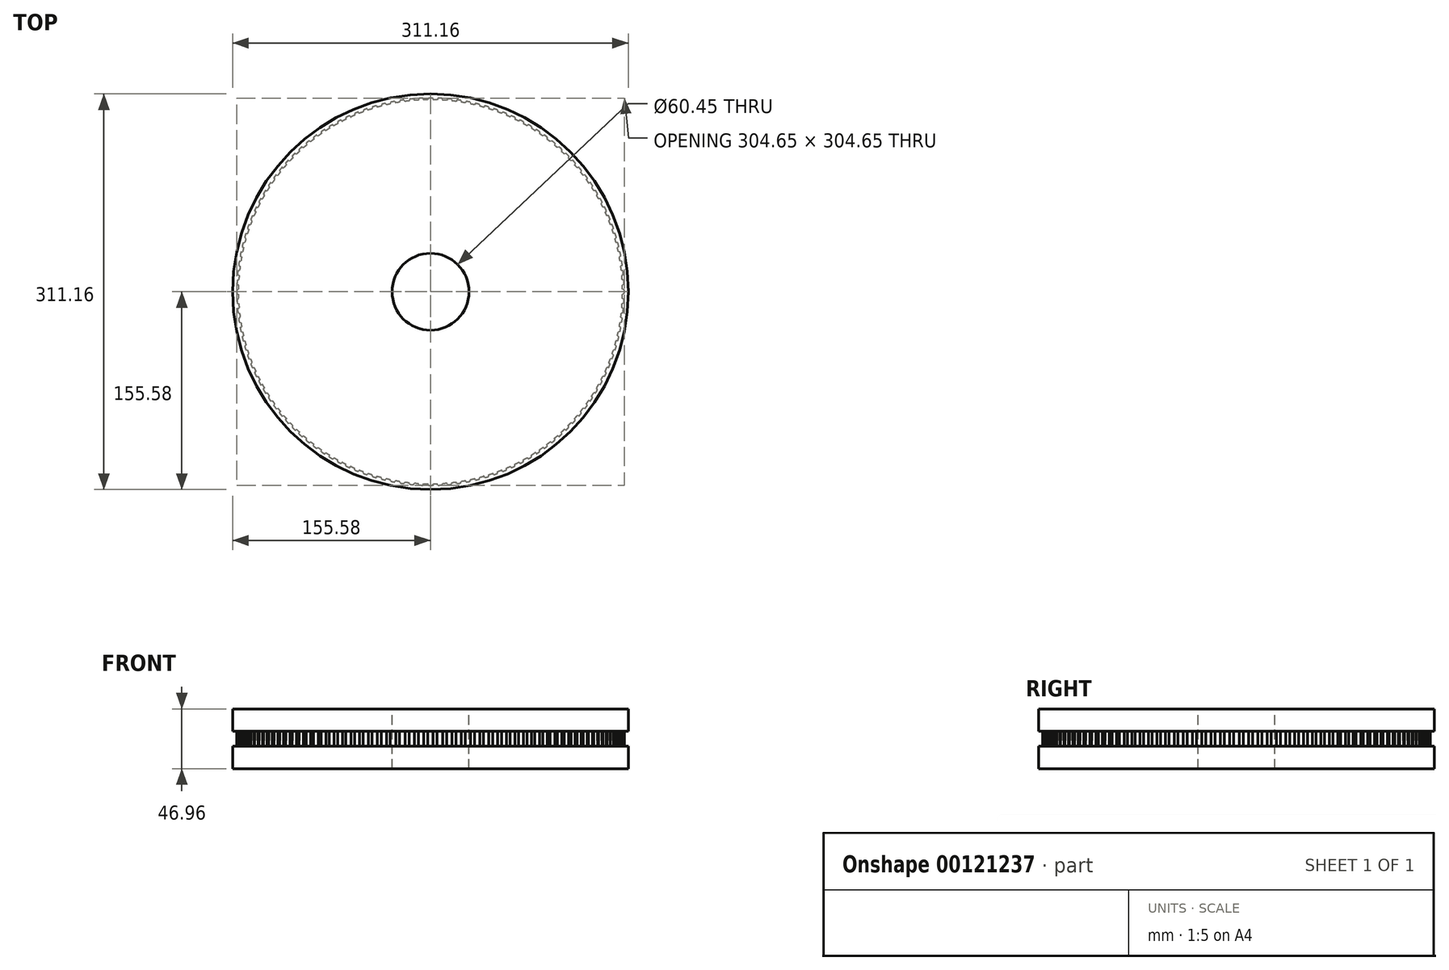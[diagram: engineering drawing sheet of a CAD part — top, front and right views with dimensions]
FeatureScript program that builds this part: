
annotation { "Feature Type Name" : "Feature", "Feature Type Description" : "" }
export const myFeature = defineFeature(function(context is Context, id is Id, definition is map)
    precondition{}
    {
        {
            var Q0;
            Q0=qCreatedBy(makeId("Top.planeOp"),FACE);
            var sketch = newSketch(context, id + "F0", { "sketchPlane" : qUnion([Q0])});
            skCircle(sketch, "E0", {"center": v(0, 0) * mm, "radius": 151 * mm});
            skSolve(sketch);
        }
        {
            var Q0;
            Q0=qSketchRegion(id+"F0",true);
            extrude(context, id + "F1", {"entities" : qUnion([Q0]), "depth" : 11.9 * mm});
        }
        {
            var Q0;
            Q0=qCreatedBy(makeId("Top.planeOp"),FACE);
            var sketch = newSketch(context, id + "F2", { "sketchPlane" : qUnion([Q0])});
            skLineSegment(sketch, "E1", {"start": v(0, -0.08) * mm, "end": v(0, 183.08) * mm, "construction": true});
            skArc(sketch, "E2", {"start": v(1.26, 152.32) * mm, "mid": v(0, 152.32) * mm, "end": v(-1.26, 152.32) * mm});
            skLineSegment(sketch, "E3", {"start": v(-1.6, 152.1) * mm, "end": v(-2.1, 151.02) * mm});
            skLineSegment(sketch, "E4", {"start": v(1.6, 152.1) * mm, "end": v(2.1, 151.02) * mm});
            skPoint(sketch, "E5.visualSharp", {"position": v(-1.5, 152.32) * mm});
            skArc(sketch, "E5.filletArc", {"start": v(-1.26, 152.32) * mm, "mid": v(-1.46, 152.26) * mm, "end": v(-1.6, 152.1) * mm});
            skPoint(sketch, "E6.visualSharp", {"position": v(1.5, 152.32) * mm});
            skArc(sketch, "E6.filletArc", {"start": v(1.6, 152.1) * mm, "mid": v(1.46, 152.26) * mm, "end": v(1.26, 152.32) * mm});
            skArc(sketch, "E7", {"start": v(-2.27, 150.9) * mm, "mid": v(-2.17, 150.94) * mm, "end": v(-2.1, 151.02) * mm});
            skArc(sketch, "E8", {"start": v(2.1, 151.02) * mm, "mid": v(2.17, 150.94) * mm, "end": v(2.27, 150.9) * mm});
            skPoint(sketch, "E9.orphan", {"position": v(2.15, 150.91) * mm});
            skArc(sketch, "E10", {"start": v(-2.27, 150.9) * mm, "mid": v(0, 150.67) * mm, "end": v(2.27, 150.9) * mm});
            skSolve(sketch);
        }
        {
            var Q0;
            Q0=makeQuery(id+"F2.imprint","IMPRINT",FACE,{"disambiguationData":[TD([[makeQuery(id+"F2.imprint","IMPRINT",EDGE,{"derivedFrom":sQuery(id+"F2.wireOp",EDGE,"E2")}),1.0]])]});
            var Q1;
            Q1=makeQuery(id+"F2.imprint","IMPRINT",FACE,{"disambiguationData":[TD([[makeQuery(id+"F2.imprint","IMPRINT",EDGE,{"derivedFrom":sQuery(id+"F2.wireOp",EDGE,"bbfa1fc5-6552-4957-9194-8f10230bb92c.0")}),1.0]])]});
            var Q2;
            Q2=makeQuery(id+"F1.opExtrude","CAP_FACE",FACE,{"disambiguationData":[OSD([sQuery(id+"F0.wireOp",EDGE,"E0")])],"isStart":false});
            extrude(context, id + "F3", {"entities" : qUnion([Q0, Q1]), "endBound" : BoundingType.UP_TO_SURFACE, "endBoundEntityFace" : qUnion([Q2]), "depth" : 25.4 * mm});
        }
        {
            var Q0;
            Q0=qCreatedBy(makeId("Front.planeOp"),FACE);
            var sketch = newSketch(context, id + "F4", { "sketchPlane" : qUnion([Q0])});
            skLineSegment(sketch, "E11", {"start": v(0, 74.48) * mm, "end": v(0, -67.78) * mm, "construction": true});
            skSolve(sketch);
        }
        {
            var Q0;
            Q0=makeQuery(id+"F3.opExtrude","SWEPT_BODY",BODY,{"disambiguationData":[OSD([sQuery(id+"F2.wireOp",EDGE,"E2"),sQuery(id+"F2.wireOp",EDGE,"E3"),sQuery(id+"F2.wireOp",EDGE,"E4"),sQuery(id+"F2.wireOp",EDGE,"E5.filletArc"),sQuery(id+"F2.wireOp",EDGE,"E6.filletArc"),sQuery(id+"F2.wireOp",EDGE,"E7"),sQuery(id+"F2.wireOp",EDGE,"E8"),sQuery(id+"F2.wireOp",EDGE,"E10")])]});
            var Q1;
            Q1=sQuery(id+"F4.wireOp",EDGE,"E11");
            circularPattern(context, id + "F5", {"entities" : qUnion([Q0]), "axis" : qUnion([Q1]), "angle" : 360 * degree, "instanceCount" : 128, "equalSpace" : true});
        }
        {
            var Q0;
            Q0=makeQuery(id+"F1.opExtrude","SWEPT_BODY",BODY,{"disambiguationData":[OSD([sQuery(id+"F0.wireOp",EDGE,"E0")])]});
            var Q1;
            Q1=makeQuery(id+"F3.opExtrude","SWEPT_BODY",BODY,{"disambiguationData":[OSD([sQuery(id+"F2.wireOp",EDGE,"E2"),sQuery(id+"F2.wireOp",EDGE,"E3"),sQuery(id+"F2.wireOp",EDGE,"E4"),sQuery(id+"F2.wireOp",EDGE,"E5.filletArc"),sQuery(id+"F2.wireOp",EDGE,"E6.filletArc"),sQuery(id+"F2.wireOp",EDGE,"E7"),sQuery(id+"F2.wireOp",EDGE,"E8"),sQuery(id+"F2.wireOp",EDGE,"E10")])]});
            var Q2;
            Q2=makeQuery(id+"F5.opPattern","COPY",BODY,{"derivedFrom":makeQuery(id+"F3.opExtrude","SWEPT_BODY",BODY,{"disambiguationData":[OSD([sQuery(id+"F2.wireOp",EDGE,"E2"),sQuery(id+"F2.wireOp",EDGE,"E3"),sQuery(id+"F2.wireOp",EDGE,"E4"),sQuery(id+"F2.wireOp",EDGE,"E5.filletArc"),sQuery(id+"F2.wireOp",EDGE,"E6.filletArc"),sQuery(id+"F2.wireOp",EDGE,"E7"),sQuery(id+"F2.wireOp",EDGE,"E8"),sQuery(id+"F2.wireOp",EDGE,"E10")])]}),"instanceName":"1"});
            var Q3;
            Q3=makeQuery(id+"F5.opPattern","COPY",BODY,{"derivedFrom":makeQuery(id+"F3.opExtrude","SWEPT_BODY",BODY,{"disambiguationData":[OSD([sQuery(id+"F2.wireOp",EDGE,"E2"),sQuery(id+"F2.wireOp",EDGE,"E3"),sQuery(id+"F2.wireOp",EDGE,"E4"),sQuery(id+"F2.wireOp",EDGE,"E5.filletArc"),sQuery(id+"F2.wireOp",EDGE,"E6.filletArc"),sQuery(id+"F2.wireOp",EDGE,"E7"),sQuery(id+"F2.wireOp",EDGE,"E8"),sQuery(id+"F2.wireOp",EDGE,"E10")])]}),"instanceName":"2"});
            var Q4;
            Q4=makeQuery(id+"F5.opPattern","COPY",BODY,{"derivedFrom":makeQuery(id+"F3.opExtrude","SWEPT_BODY",BODY,{"disambiguationData":[OSD([sQuery(id+"F2.wireOp",EDGE,"E2"),sQuery(id+"F2.wireOp",EDGE,"E3"),sQuery(id+"F2.wireOp",EDGE,"E4"),sQuery(id+"F2.wireOp",EDGE,"E5.filletArc"),sQuery(id+"F2.wireOp",EDGE,"E6.filletArc"),sQuery(id+"F2.wireOp",EDGE,"E7"),sQuery(id+"F2.wireOp",EDGE,"E8"),sQuery(id+"F2.wireOp",EDGE,"E10")])]}),"instanceName":"3"});
            var Q5;
            Q5=makeQuery(id+"F5.opPattern","COPY",BODY,{"derivedFrom":makeQuery(id+"F3.opExtrude","SWEPT_BODY",BODY,{"disambiguationData":[OSD([sQuery(id+"F2.wireOp",EDGE,"E2"),sQuery(id+"F2.wireOp",EDGE,"E3"),sQuery(id+"F2.wireOp",EDGE,"E4"),sQuery(id+"F2.wireOp",EDGE,"E5.filletArc"),sQuery(id+"F2.wireOp",EDGE,"E6.filletArc"),sQuery(id+"F2.wireOp",EDGE,"E7"),sQuery(id+"F2.wireOp",EDGE,"E8"),sQuery(id+"F2.wireOp",EDGE,"E10")])]}),"instanceName":"4"});
            var Q6;
            Q6=makeQuery(id+"F5.opPattern","COPY",BODY,{"derivedFrom":makeQuery(id+"F3.opExtrude","SWEPT_BODY",BODY,{"disambiguationData":[OSD([sQuery(id+"F2.wireOp",EDGE,"E2"),sQuery(id+"F2.wireOp",EDGE,"E3"),sQuery(id+"F2.wireOp",EDGE,"E4"),sQuery(id+"F2.wireOp",EDGE,"E5.filletArc"),sQuery(id+"F2.wireOp",EDGE,"E6.filletArc"),sQuery(id+"F2.wireOp",EDGE,"E7"),sQuery(id+"F2.wireOp",EDGE,"E8"),sQuery(id+"F2.wireOp",EDGE,"E10")])]}),"instanceName":"5"});
            var Q7;
            Q7=makeQuery(id+"F5.opPattern","COPY",BODY,{"derivedFrom":makeQuery(id+"F3.opExtrude","SWEPT_BODY",BODY,{"disambiguationData":[OSD([sQuery(id+"F2.wireOp",EDGE,"E2"),sQuery(id+"F2.wireOp",EDGE,"E3"),sQuery(id+"F2.wireOp",EDGE,"E4"),sQuery(id+"F2.wireOp",EDGE,"E5.filletArc"),sQuery(id+"F2.wireOp",EDGE,"E6.filletArc"),sQuery(id+"F2.wireOp",EDGE,"E7"),sQuery(id+"F2.wireOp",EDGE,"E8"),sQuery(id+"F2.wireOp",EDGE,"E10")])]}),"instanceName":"6"});
            var Q8;
            Q8=makeQuery(id+"F5.opPattern","COPY",BODY,{"derivedFrom":makeQuery(id+"F3.opExtrude","SWEPT_BODY",BODY,{"disambiguationData":[OSD([sQuery(id+"F2.wireOp",EDGE,"E2"),sQuery(id+"F2.wireOp",EDGE,"E3"),sQuery(id+"F2.wireOp",EDGE,"E4"),sQuery(id+"F2.wireOp",EDGE,"E5.filletArc"),sQuery(id+"F2.wireOp",EDGE,"E6.filletArc"),sQuery(id+"F2.wireOp",EDGE,"E7"),sQuery(id+"F2.wireOp",EDGE,"E8"),sQuery(id+"F2.wireOp",EDGE,"E10")])]}),"instanceName":"7"});
            var Q9;
            Q9=makeQuery(id+"F5.opPattern","COPY",BODY,{"derivedFrom":makeQuery(id+"F3.opExtrude","SWEPT_BODY",BODY,{"disambiguationData":[OSD([sQuery(id+"F2.wireOp",EDGE,"E2"),sQuery(id+"F2.wireOp",EDGE,"E3"),sQuery(id+"F2.wireOp",EDGE,"E4"),sQuery(id+"F2.wireOp",EDGE,"E5.filletArc"),sQuery(id+"F2.wireOp",EDGE,"E6.filletArc"),sQuery(id+"F2.wireOp",EDGE,"E7"),sQuery(id+"F2.wireOp",EDGE,"E8"),sQuery(id+"F2.wireOp",EDGE,"E10")])]}),"instanceName":"8"});
            var Q10;
            Q10=makeQuery(id+"F5.opPattern","COPY",BODY,{"derivedFrom":makeQuery(id+"F3.opExtrude","SWEPT_BODY",BODY,{"disambiguationData":[OSD([sQuery(id+"F2.wireOp",EDGE,"E2"),sQuery(id+"F2.wireOp",EDGE,"E3"),sQuery(id+"F2.wireOp",EDGE,"E4"),sQuery(id+"F2.wireOp",EDGE,"E5.filletArc"),sQuery(id+"F2.wireOp",EDGE,"E6.filletArc"),sQuery(id+"F2.wireOp",EDGE,"E7"),sQuery(id+"F2.wireOp",EDGE,"E8"),sQuery(id+"F2.wireOp",EDGE,"E10")])]}),"instanceName":"9"});
            var Q11;
            Q11=makeQuery(id+"F5.opPattern","COPY",BODY,{"derivedFrom":makeQuery(id+"F3.opExtrude","SWEPT_BODY",BODY,{"disambiguationData":[OSD([sQuery(id+"F2.wireOp",EDGE,"E2"),sQuery(id+"F2.wireOp",EDGE,"E3"),sQuery(id+"F2.wireOp",EDGE,"E4"),sQuery(id+"F2.wireOp",EDGE,"E5.filletArc"),sQuery(id+"F2.wireOp",EDGE,"E6.filletArc"),sQuery(id+"F2.wireOp",EDGE,"E7"),sQuery(id+"F2.wireOp",EDGE,"E8"),sQuery(id+"F2.wireOp",EDGE,"E10")])]}),"instanceName":"10"});
            var Q12;
            Q12=makeQuery(id+"F5.opPattern","COPY",BODY,{"derivedFrom":makeQuery(id+"F3.opExtrude","SWEPT_BODY",BODY,{"disambiguationData":[OSD([sQuery(id+"F2.wireOp",EDGE,"E2"),sQuery(id+"F2.wireOp",EDGE,"E3"),sQuery(id+"F2.wireOp",EDGE,"E4"),sQuery(id+"F2.wireOp",EDGE,"E5.filletArc"),sQuery(id+"F2.wireOp",EDGE,"E6.filletArc"),sQuery(id+"F2.wireOp",EDGE,"E7"),sQuery(id+"F2.wireOp",EDGE,"E8"),sQuery(id+"F2.wireOp",EDGE,"E10")])]}),"instanceName":"11"});
            var Q13;
            Q13=makeQuery(id+"F5.opPattern","COPY",BODY,{"derivedFrom":makeQuery(id+"F3.opExtrude","SWEPT_BODY",BODY,{"disambiguationData":[OSD([sQuery(id+"F2.wireOp",EDGE,"E2"),sQuery(id+"F2.wireOp",EDGE,"E3"),sQuery(id+"F2.wireOp",EDGE,"E4"),sQuery(id+"F2.wireOp",EDGE,"E5.filletArc"),sQuery(id+"F2.wireOp",EDGE,"E6.filletArc"),sQuery(id+"F2.wireOp",EDGE,"E7"),sQuery(id+"F2.wireOp",EDGE,"E8"),sQuery(id+"F2.wireOp",EDGE,"E10")])]}),"instanceName":"12"});
            var Q14;
            Q14=makeQuery(id+"F5.opPattern","COPY",BODY,{"derivedFrom":makeQuery(id+"F3.opExtrude","SWEPT_BODY",BODY,{"disambiguationData":[OSD([sQuery(id+"F2.wireOp",EDGE,"E2"),sQuery(id+"F2.wireOp",EDGE,"E3"),sQuery(id+"F2.wireOp",EDGE,"E4"),sQuery(id+"F2.wireOp",EDGE,"E5.filletArc"),sQuery(id+"F2.wireOp",EDGE,"E6.filletArc"),sQuery(id+"F2.wireOp",EDGE,"E7"),sQuery(id+"F2.wireOp",EDGE,"E8"),sQuery(id+"F2.wireOp",EDGE,"E10")])]}),"instanceName":"13"});
            var Q15;
            Q15=makeQuery(id+"F5.opPattern","COPY",BODY,{"derivedFrom":makeQuery(id+"F3.opExtrude","SWEPT_BODY",BODY,{"disambiguationData":[OSD([sQuery(id+"F2.wireOp",EDGE,"E2"),sQuery(id+"F2.wireOp",EDGE,"E3"),sQuery(id+"F2.wireOp",EDGE,"E4"),sQuery(id+"F2.wireOp",EDGE,"E5.filletArc"),sQuery(id+"F2.wireOp",EDGE,"E6.filletArc"),sQuery(id+"F2.wireOp",EDGE,"E7"),sQuery(id+"F2.wireOp",EDGE,"E8"),sQuery(id+"F2.wireOp",EDGE,"E10")])]}),"instanceName":"14"});
            var Q16;
            Q16=makeQuery(id+"F5.opPattern","COPY",BODY,{"derivedFrom":makeQuery(id+"F3.opExtrude","SWEPT_BODY",BODY,{"disambiguationData":[OSD([sQuery(id+"F2.wireOp",EDGE,"E2"),sQuery(id+"F2.wireOp",EDGE,"E3"),sQuery(id+"F2.wireOp",EDGE,"E4"),sQuery(id+"F2.wireOp",EDGE,"E5.filletArc"),sQuery(id+"F2.wireOp",EDGE,"E6.filletArc"),sQuery(id+"F2.wireOp",EDGE,"E7"),sQuery(id+"F2.wireOp",EDGE,"E8"),sQuery(id+"F2.wireOp",EDGE,"E10")])]}),"instanceName":"15"});
            var Q17;
            Q17=makeQuery(id+"F5.opPattern","COPY",BODY,{"derivedFrom":makeQuery(id+"F3.opExtrude","SWEPT_BODY",BODY,{"disambiguationData":[OSD([sQuery(id+"F2.wireOp",EDGE,"E2"),sQuery(id+"F2.wireOp",EDGE,"E3"),sQuery(id+"F2.wireOp",EDGE,"E4"),sQuery(id+"F2.wireOp",EDGE,"E5.filletArc"),sQuery(id+"F2.wireOp",EDGE,"E6.filletArc"),sQuery(id+"F2.wireOp",EDGE,"E7"),sQuery(id+"F2.wireOp",EDGE,"E8"),sQuery(id+"F2.wireOp",EDGE,"E10")])]}),"instanceName":"16"});
            var Q18;
            Q18=makeQuery(id+"F5.opPattern","COPY",BODY,{"derivedFrom":makeQuery(id+"F3.opExtrude","SWEPT_BODY",BODY,{"disambiguationData":[OSD([sQuery(id+"F2.wireOp",EDGE,"E2"),sQuery(id+"F2.wireOp",EDGE,"E3"),sQuery(id+"F2.wireOp",EDGE,"E4"),sQuery(id+"F2.wireOp",EDGE,"E5.filletArc"),sQuery(id+"F2.wireOp",EDGE,"E6.filletArc"),sQuery(id+"F2.wireOp",EDGE,"E7"),sQuery(id+"F2.wireOp",EDGE,"E8"),sQuery(id+"F2.wireOp",EDGE,"E10")])]}),"instanceName":"17"});
            var Q19;
            Q19=makeQuery(id+"F5.opPattern","COPY",BODY,{"derivedFrom":makeQuery(id+"F3.opExtrude","SWEPT_BODY",BODY,{"disambiguationData":[OSD([sQuery(id+"F2.wireOp",EDGE,"E2"),sQuery(id+"F2.wireOp",EDGE,"E3"),sQuery(id+"F2.wireOp",EDGE,"E4"),sQuery(id+"F2.wireOp",EDGE,"E5.filletArc"),sQuery(id+"F2.wireOp",EDGE,"E6.filletArc"),sQuery(id+"F2.wireOp",EDGE,"E7"),sQuery(id+"F2.wireOp",EDGE,"E8"),sQuery(id+"F2.wireOp",EDGE,"E10")])]}),"instanceName":"18"});
            var Q20;
            Q20=makeQuery(id+"F5.opPattern","COPY",BODY,{"derivedFrom":makeQuery(id+"F3.opExtrude","SWEPT_BODY",BODY,{"disambiguationData":[OSD([sQuery(id+"F2.wireOp",EDGE,"E2"),sQuery(id+"F2.wireOp",EDGE,"E3"),sQuery(id+"F2.wireOp",EDGE,"E4"),sQuery(id+"F2.wireOp",EDGE,"E5.filletArc"),sQuery(id+"F2.wireOp",EDGE,"E6.filletArc"),sQuery(id+"F2.wireOp",EDGE,"E7"),sQuery(id+"F2.wireOp",EDGE,"E8"),sQuery(id+"F2.wireOp",EDGE,"E10")])]}),"instanceName":"19"});
            var Q21;
            Q21=makeQuery(id+"F5.opPattern","COPY",BODY,{"derivedFrom":makeQuery(id+"F3.opExtrude","SWEPT_BODY",BODY,{"disambiguationData":[OSD([sQuery(id+"F2.wireOp",EDGE,"E2"),sQuery(id+"F2.wireOp",EDGE,"E3"),sQuery(id+"F2.wireOp",EDGE,"E4"),sQuery(id+"F2.wireOp",EDGE,"E5.filletArc"),sQuery(id+"F2.wireOp",EDGE,"E6.filletArc"),sQuery(id+"F2.wireOp",EDGE,"E7"),sQuery(id+"F2.wireOp",EDGE,"E8"),sQuery(id+"F2.wireOp",EDGE,"E10")])]}),"instanceName":"20"});
            var Q22;
            Q22=makeQuery(id+"F5.opPattern","COPY",BODY,{"derivedFrom":makeQuery(id+"F3.opExtrude","SWEPT_BODY",BODY,{"disambiguationData":[OSD([sQuery(id+"F2.wireOp",EDGE,"E2"),sQuery(id+"F2.wireOp",EDGE,"E3"),sQuery(id+"F2.wireOp",EDGE,"E4"),sQuery(id+"F2.wireOp",EDGE,"E5.filletArc"),sQuery(id+"F2.wireOp",EDGE,"E6.filletArc"),sQuery(id+"F2.wireOp",EDGE,"E7"),sQuery(id+"F2.wireOp",EDGE,"E8"),sQuery(id+"F2.wireOp",EDGE,"E10")])]}),"instanceName":"21"});
            var Q23;
            Q23=makeQuery(id+"F5.opPattern","COPY",BODY,{"derivedFrom":makeQuery(id+"F3.opExtrude","SWEPT_BODY",BODY,{"disambiguationData":[OSD([sQuery(id+"F2.wireOp",EDGE,"E2"),sQuery(id+"F2.wireOp",EDGE,"E3"),sQuery(id+"F2.wireOp",EDGE,"E4"),sQuery(id+"F2.wireOp",EDGE,"E5.filletArc"),sQuery(id+"F2.wireOp",EDGE,"E6.filletArc"),sQuery(id+"F2.wireOp",EDGE,"E7"),sQuery(id+"F2.wireOp",EDGE,"E8"),sQuery(id+"F2.wireOp",EDGE,"E10")])]}),"instanceName":"22"});
            var Q24;
            Q24=makeQuery(id+"F5.opPattern","COPY",BODY,{"derivedFrom":makeQuery(id+"F3.opExtrude","SWEPT_BODY",BODY,{"disambiguationData":[OSD([sQuery(id+"F2.wireOp",EDGE,"E2"),sQuery(id+"F2.wireOp",EDGE,"E3"),sQuery(id+"F2.wireOp",EDGE,"E4"),sQuery(id+"F2.wireOp",EDGE,"E5.filletArc"),sQuery(id+"F2.wireOp",EDGE,"E6.filletArc"),sQuery(id+"F2.wireOp",EDGE,"E7"),sQuery(id+"F2.wireOp",EDGE,"E8"),sQuery(id+"F2.wireOp",EDGE,"E10")])]}),"instanceName":"23"});
            var Q25;
            Q25=makeQuery(id+"F5.opPattern","COPY",BODY,{"derivedFrom":makeQuery(id+"F3.opExtrude","SWEPT_BODY",BODY,{"disambiguationData":[OSD([sQuery(id+"F2.wireOp",EDGE,"E2"),sQuery(id+"F2.wireOp",EDGE,"E3"),sQuery(id+"F2.wireOp",EDGE,"E4"),sQuery(id+"F2.wireOp",EDGE,"E5.filletArc"),sQuery(id+"F2.wireOp",EDGE,"E6.filletArc"),sQuery(id+"F2.wireOp",EDGE,"E7"),sQuery(id+"F2.wireOp",EDGE,"E8"),sQuery(id+"F2.wireOp",EDGE,"E10")])]}),"instanceName":"24"});
            var Q26;
            Q26=makeQuery(id+"F5.opPattern","COPY",BODY,{"derivedFrom":makeQuery(id+"F3.opExtrude","SWEPT_BODY",BODY,{"disambiguationData":[OSD([sQuery(id+"F2.wireOp",EDGE,"E2"),sQuery(id+"F2.wireOp",EDGE,"E3"),sQuery(id+"F2.wireOp",EDGE,"E4"),sQuery(id+"F2.wireOp",EDGE,"E5.filletArc"),sQuery(id+"F2.wireOp",EDGE,"E6.filletArc"),sQuery(id+"F2.wireOp",EDGE,"E7"),sQuery(id+"F2.wireOp",EDGE,"E8"),sQuery(id+"F2.wireOp",EDGE,"E10")])]}),"instanceName":"25"});
            var Q27;
            Q27=makeQuery(id+"F5.opPattern","COPY",BODY,{"derivedFrom":makeQuery(id+"F3.opExtrude","SWEPT_BODY",BODY,{"disambiguationData":[OSD([sQuery(id+"F2.wireOp",EDGE,"E2"),sQuery(id+"F2.wireOp",EDGE,"E3"),sQuery(id+"F2.wireOp",EDGE,"E4"),sQuery(id+"F2.wireOp",EDGE,"E5.filletArc"),sQuery(id+"F2.wireOp",EDGE,"E6.filletArc"),sQuery(id+"F2.wireOp",EDGE,"E7"),sQuery(id+"F2.wireOp",EDGE,"E8"),sQuery(id+"F2.wireOp",EDGE,"E10")])]}),"instanceName":"26"});
            var Q28;
            Q28=makeQuery(id+"F5.opPattern","COPY",BODY,{"derivedFrom":makeQuery(id+"F3.opExtrude","SWEPT_BODY",BODY,{"disambiguationData":[OSD([sQuery(id+"F2.wireOp",EDGE,"E2"),sQuery(id+"F2.wireOp",EDGE,"E3"),sQuery(id+"F2.wireOp",EDGE,"E4"),sQuery(id+"F2.wireOp",EDGE,"E5.filletArc"),sQuery(id+"F2.wireOp",EDGE,"E6.filletArc"),sQuery(id+"F2.wireOp",EDGE,"E7"),sQuery(id+"F2.wireOp",EDGE,"E8"),sQuery(id+"F2.wireOp",EDGE,"E10")])]}),"instanceName":"27"});
            var Q29;
            Q29=makeQuery(id+"F5.opPattern","COPY",BODY,{"derivedFrom":makeQuery(id+"F3.opExtrude","SWEPT_BODY",BODY,{"disambiguationData":[OSD([sQuery(id+"F2.wireOp",EDGE,"E2"),sQuery(id+"F2.wireOp",EDGE,"E3"),sQuery(id+"F2.wireOp",EDGE,"E4"),sQuery(id+"F2.wireOp",EDGE,"E5.filletArc"),sQuery(id+"F2.wireOp",EDGE,"E6.filletArc"),sQuery(id+"F2.wireOp",EDGE,"E7"),sQuery(id+"F2.wireOp",EDGE,"E8"),sQuery(id+"F2.wireOp",EDGE,"E10")])]}),"instanceName":"28"});
            var Q30;
            Q30=makeQuery(id+"F5.opPattern","COPY",BODY,{"derivedFrom":makeQuery(id+"F3.opExtrude","SWEPT_BODY",BODY,{"disambiguationData":[OSD([sQuery(id+"F2.wireOp",EDGE,"E2"),sQuery(id+"F2.wireOp",EDGE,"E3"),sQuery(id+"F2.wireOp",EDGE,"E4"),sQuery(id+"F2.wireOp",EDGE,"E5.filletArc"),sQuery(id+"F2.wireOp",EDGE,"E6.filletArc"),sQuery(id+"F2.wireOp",EDGE,"E7"),sQuery(id+"F2.wireOp",EDGE,"E8"),sQuery(id+"F2.wireOp",EDGE,"E10")])]}),"instanceName":"29"});
            var Q31;
            Q31=makeQuery(id+"F5.opPattern","COPY",BODY,{"derivedFrom":makeQuery(id+"F3.opExtrude","SWEPT_BODY",BODY,{"disambiguationData":[OSD([sQuery(id+"F2.wireOp",EDGE,"E2"),sQuery(id+"F2.wireOp",EDGE,"E3"),sQuery(id+"F2.wireOp",EDGE,"E4"),sQuery(id+"F2.wireOp",EDGE,"E5.filletArc"),sQuery(id+"F2.wireOp",EDGE,"E6.filletArc"),sQuery(id+"F2.wireOp",EDGE,"E7"),sQuery(id+"F2.wireOp",EDGE,"E8"),sQuery(id+"F2.wireOp",EDGE,"E10")])]}),"instanceName":"30"});
            var Q32;
            Q32=makeQuery(id+"F5.opPattern","COPY",BODY,{"derivedFrom":makeQuery(id+"F3.opExtrude","SWEPT_BODY",BODY,{"disambiguationData":[OSD([sQuery(id+"F2.wireOp",EDGE,"E2"),sQuery(id+"F2.wireOp",EDGE,"E3"),sQuery(id+"F2.wireOp",EDGE,"E4"),sQuery(id+"F2.wireOp",EDGE,"E5.filletArc"),sQuery(id+"F2.wireOp",EDGE,"E6.filletArc"),sQuery(id+"F2.wireOp",EDGE,"E7"),sQuery(id+"F2.wireOp",EDGE,"E8"),sQuery(id+"F2.wireOp",EDGE,"E10")])]}),"instanceName":"31"});
            var Q33;
            Q33=makeQuery(id+"F5.opPattern","COPY",BODY,{"derivedFrom":makeQuery(id+"F3.opExtrude","SWEPT_BODY",BODY,{"disambiguationData":[OSD([sQuery(id+"F2.wireOp",EDGE,"E2"),sQuery(id+"F2.wireOp",EDGE,"E3"),sQuery(id+"F2.wireOp",EDGE,"E4"),sQuery(id+"F2.wireOp",EDGE,"E5.filletArc"),sQuery(id+"F2.wireOp",EDGE,"E6.filletArc"),sQuery(id+"F2.wireOp",EDGE,"E7"),sQuery(id+"F2.wireOp",EDGE,"E8"),sQuery(id+"F2.wireOp",EDGE,"E10")])]}),"instanceName":"32"});
            var Q34;
            Q34=makeQuery(id+"F5.opPattern","COPY",BODY,{"derivedFrom":makeQuery(id+"F3.opExtrude","SWEPT_BODY",BODY,{"disambiguationData":[OSD([sQuery(id+"F2.wireOp",EDGE,"E2"),sQuery(id+"F2.wireOp",EDGE,"E3"),sQuery(id+"F2.wireOp",EDGE,"E4"),sQuery(id+"F2.wireOp",EDGE,"E5.filletArc"),sQuery(id+"F2.wireOp",EDGE,"E6.filletArc"),sQuery(id+"F2.wireOp",EDGE,"E7"),sQuery(id+"F2.wireOp",EDGE,"E8"),sQuery(id+"F2.wireOp",EDGE,"E10")])]}),"instanceName":"33"});
            var Q35;
            Q35=makeQuery(id+"F5.opPattern","COPY",BODY,{"derivedFrom":makeQuery(id+"F3.opExtrude","SWEPT_BODY",BODY,{"disambiguationData":[OSD([sQuery(id+"F2.wireOp",EDGE,"E2"),sQuery(id+"F2.wireOp",EDGE,"E3"),sQuery(id+"F2.wireOp",EDGE,"E4"),sQuery(id+"F2.wireOp",EDGE,"E5.filletArc"),sQuery(id+"F2.wireOp",EDGE,"E6.filletArc"),sQuery(id+"F2.wireOp",EDGE,"E7"),sQuery(id+"F2.wireOp",EDGE,"E8"),sQuery(id+"F2.wireOp",EDGE,"E10")])]}),"instanceName":"34"});
            var Q36;
            Q36=makeQuery(id+"F5.opPattern","COPY",BODY,{"derivedFrom":makeQuery(id+"F3.opExtrude","SWEPT_BODY",BODY,{"disambiguationData":[OSD([sQuery(id+"F2.wireOp",EDGE,"E2"),sQuery(id+"F2.wireOp",EDGE,"E3"),sQuery(id+"F2.wireOp",EDGE,"E4"),sQuery(id+"F2.wireOp",EDGE,"E5.filletArc"),sQuery(id+"F2.wireOp",EDGE,"E6.filletArc"),sQuery(id+"F2.wireOp",EDGE,"E7"),sQuery(id+"F2.wireOp",EDGE,"E8"),sQuery(id+"F2.wireOp",EDGE,"E10")])]}),"instanceName":"35"});
            var Q37;
            Q37=makeQuery(id+"F5.opPattern","COPY",BODY,{"derivedFrom":makeQuery(id+"F3.opExtrude","SWEPT_BODY",BODY,{"disambiguationData":[OSD([sQuery(id+"F2.wireOp",EDGE,"E2"),sQuery(id+"F2.wireOp",EDGE,"E3"),sQuery(id+"F2.wireOp",EDGE,"E4"),sQuery(id+"F2.wireOp",EDGE,"E5.filletArc"),sQuery(id+"F2.wireOp",EDGE,"E6.filletArc"),sQuery(id+"F2.wireOp",EDGE,"E7"),sQuery(id+"F2.wireOp",EDGE,"E8"),sQuery(id+"F2.wireOp",EDGE,"E10")])]}),"instanceName":"36"});
            var Q38;
            Q38=makeQuery(id+"F5.opPattern","COPY",BODY,{"derivedFrom":makeQuery(id+"F3.opExtrude","SWEPT_BODY",BODY,{"disambiguationData":[OSD([sQuery(id+"F2.wireOp",EDGE,"E2"),sQuery(id+"F2.wireOp",EDGE,"E3"),sQuery(id+"F2.wireOp",EDGE,"E4"),sQuery(id+"F2.wireOp",EDGE,"E5.filletArc"),sQuery(id+"F2.wireOp",EDGE,"E6.filletArc"),sQuery(id+"F2.wireOp",EDGE,"E7"),sQuery(id+"F2.wireOp",EDGE,"E8"),sQuery(id+"F2.wireOp",EDGE,"E10")])]}),"instanceName":"37"});
            var Q39;
            Q39=makeQuery(id+"F5.opPattern","COPY",BODY,{"derivedFrom":makeQuery(id+"F3.opExtrude","SWEPT_BODY",BODY,{"disambiguationData":[OSD([sQuery(id+"F2.wireOp",EDGE,"E2"),sQuery(id+"F2.wireOp",EDGE,"E3"),sQuery(id+"F2.wireOp",EDGE,"E4"),sQuery(id+"F2.wireOp",EDGE,"E5.filletArc"),sQuery(id+"F2.wireOp",EDGE,"E6.filletArc"),sQuery(id+"F2.wireOp",EDGE,"E7"),sQuery(id+"F2.wireOp",EDGE,"E8"),sQuery(id+"F2.wireOp",EDGE,"E10")])]}),"instanceName":"38"});
            var Q40;
            Q40=makeQuery(id+"F5.opPattern","COPY",BODY,{"derivedFrom":makeQuery(id+"F3.opExtrude","SWEPT_BODY",BODY,{"disambiguationData":[OSD([sQuery(id+"F2.wireOp",EDGE,"E2"),sQuery(id+"F2.wireOp",EDGE,"E3"),sQuery(id+"F2.wireOp",EDGE,"E4"),sQuery(id+"F2.wireOp",EDGE,"E5.filletArc"),sQuery(id+"F2.wireOp",EDGE,"E6.filletArc"),sQuery(id+"F2.wireOp",EDGE,"E7"),sQuery(id+"F2.wireOp",EDGE,"E8"),sQuery(id+"F2.wireOp",EDGE,"E10")])]}),"instanceName":"39"});
            var Q41;
            Q41=makeQuery(id+"F5.opPattern","COPY",BODY,{"derivedFrom":makeQuery(id+"F3.opExtrude","SWEPT_BODY",BODY,{"disambiguationData":[OSD([sQuery(id+"F2.wireOp",EDGE,"E2"),sQuery(id+"F2.wireOp",EDGE,"E3"),sQuery(id+"F2.wireOp",EDGE,"E4"),sQuery(id+"F2.wireOp",EDGE,"E5.filletArc"),sQuery(id+"F2.wireOp",EDGE,"E6.filletArc"),sQuery(id+"F2.wireOp",EDGE,"E7"),sQuery(id+"F2.wireOp",EDGE,"E8"),sQuery(id+"F2.wireOp",EDGE,"E10")])]}),"instanceName":"40"});
            var Q42;
            Q42=makeQuery(id+"F5.opPattern","COPY",BODY,{"derivedFrom":makeQuery(id+"F3.opExtrude","SWEPT_BODY",BODY,{"disambiguationData":[OSD([sQuery(id+"F2.wireOp",EDGE,"E2"),sQuery(id+"F2.wireOp",EDGE,"E3"),sQuery(id+"F2.wireOp",EDGE,"E4"),sQuery(id+"F2.wireOp",EDGE,"E5.filletArc"),sQuery(id+"F2.wireOp",EDGE,"E6.filletArc"),sQuery(id+"F2.wireOp",EDGE,"E7"),sQuery(id+"F2.wireOp",EDGE,"E8"),sQuery(id+"F2.wireOp",EDGE,"E10")])]}),"instanceName":"41"});
            var Q43;
            Q43=makeQuery(id+"F5.opPattern","COPY",BODY,{"derivedFrom":makeQuery(id+"F3.opExtrude","SWEPT_BODY",BODY,{"disambiguationData":[OSD([sQuery(id+"F2.wireOp",EDGE,"E2"),sQuery(id+"F2.wireOp",EDGE,"E3"),sQuery(id+"F2.wireOp",EDGE,"E4"),sQuery(id+"F2.wireOp",EDGE,"E5.filletArc"),sQuery(id+"F2.wireOp",EDGE,"E6.filletArc"),sQuery(id+"F2.wireOp",EDGE,"E7"),sQuery(id+"F2.wireOp",EDGE,"E8"),sQuery(id+"F2.wireOp",EDGE,"E10")])]}),"instanceName":"42"});
            var Q44;
            Q44=makeQuery(id+"F5.opPattern","COPY",BODY,{"derivedFrom":makeQuery(id+"F3.opExtrude","SWEPT_BODY",BODY,{"disambiguationData":[OSD([sQuery(id+"F2.wireOp",EDGE,"E2"),sQuery(id+"F2.wireOp",EDGE,"E3"),sQuery(id+"F2.wireOp",EDGE,"E4"),sQuery(id+"F2.wireOp",EDGE,"E5.filletArc"),sQuery(id+"F2.wireOp",EDGE,"E6.filletArc"),sQuery(id+"F2.wireOp",EDGE,"E7"),sQuery(id+"F2.wireOp",EDGE,"E8"),sQuery(id+"F2.wireOp",EDGE,"E10")])]}),"instanceName":"43"});
            var Q45;
            Q45=makeQuery(id+"F5.opPattern","COPY",BODY,{"derivedFrom":makeQuery(id+"F3.opExtrude","SWEPT_BODY",BODY,{"disambiguationData":[OSD([sQuery(id+"F2.wireOp",EDGE,"E2"),sQuery(id+"F2.wireOp",EDGE,"E3"),sQuery(id+"F2.wireOp",EDGE,"E4"),sQuery(id+"F2.wireOp",EDGE,"E5.filletArc"),sQuery(id+"F2.wireOp",EDGE,"E6.filletArc"),sQuery(id+"F2.wireOp",EDGE,"E7"),sQuery(id+"F2.wireOp",EDGE,"E8"),sQuery(id+"F2.wireOp",EDGE,"E10")])]}),"instanceName":"44"});
            var Q46;
            Q46=makeQuery(id+"F5.opPattern","COPY",BODY,{"derivedFrom":makeQuery(id+"F3.opExtrude","SWEPT_BODY",BODY,{"disambiguationData":[OSD([sQuery(id+"F2.wireOp",EDGE,"E2"),sQuery(id+"F2.wireOp",EDGE,"E3"),sQuery(id+"F2.wireOp",EDGE,"E4"),sQuery(id+"F2.wireOp",EDGE,"E5.filletArc"),sQuery(id+"F2.wireOp",EDGE,"E6.filletArc"),sQuery(id+"F2.wireOp",EDGE,"E7"),sQuery(id+"F2.wireOp",EDGE,"E8"),sQuery(id+"F2.wireOp",EDGE,"E10")])]}),"instanceName":"45"});
            var Q47;
            Q47=makeQuery(id+"F5.opPattern","COPY",BODY,{"derivedFrom":makeQuery(id+"F3.opExtrude","SWEPT_BODY",BODY,{"disambiguationData":[OSD([sQuery(id+"F2.wireOp",EDGE,"E2"),sQuery(id+"F2.wireOp",EDGE,"E3"),sQuery(id+"F2.wireOp",EDGE,"E4"),sQuery(id+"F2.wireOp",EDGE,"E5.filletArc"),sQuery(id+"F2.wireOp",EDGE,"E6.filletArc"),sQuery(id+"F2.wireOp",EDGE,"E7"),sQuery(id+"F2.wireOp",EDGE,"E8"),sQuery(id+"F2.wireOp",EDGE,"E10")])]}),"instanceName":"46"});
            var Q48;
            Q48=makeQuery(id+"F5.opPattern","COPY",BODY,{"derivedFrom":makeQuery(id+"F3.opExtrude","SWEPT_BODY",BODY,{"disambiguationData":[OSD([sQuery(id+"F2.wireOp",EDGE,"E2"),sQuery(id+"F2.wireOp",EDGE,"E3"),sQuery(id+"F2.wireOp",EDGE,"E4"),sQuery(id+"F2.wireOp",EDGE,"E5.filletArc"),sQuery(id+"F2.wireOp",EDGE,"E6.filletArc"),sQuery(id+"F2.wireOp",EDGE,"E7"),sQuery(id+"F2.wireOp",EDGE,"E8"),sQuery(id+"F2.wireOp",EDGE,"E10")])]}),"instanceName":"47"});
            var Q49;
            Q49=makeQuery(id+"F5.opPattern","COPY",BODY,{"derivedFrom":makeQuery(id+"F3.opExtrude","SWEPT_BODY",BODY,{"disambiguationData":[OSD([sQuery(id+"F2.wireOp",EDGE,"E2"),sQuery(id+"F2.wireOp",EDGE,"E3"),sQuery(id+"F2.wireOp",EDGE,"E4"),sQuery(id+"F2.wireOp",EDGE,"E5.filletArc"),sQuery(id+"F2.wireOp",EDGE,"E6.filletArc"),sQuery(id+"F2.wireOp",EDGE,"E7"),sQuery(id+"F2.wireOp",EDGE,"E8"),sQuery(id+"F2.wireOp",EDGE,"E10")])]}),"instanceName":"48"});
            var Q50;
            Q50=makeQuery(id+"F5.opPattern","COPY",BODY,{"derivedFrom":makeQuery(id+"F3.opExtrude","SWEPT_BODY",BODY,{"disambiguationData":[OSD([sQuery(id+"F2.wireOp",EDGE,"E2"),sQuery(id+"F2.wireOp",EDGE,"E3"),sQuery(id+"F2.wireOp",EDGE,"E4"),sQuery(id+"F2.wireOp",EDGE,"E5.filletArc"),sQuery(id+"F2.wireOp",EDGE,"E6.filletArc"),sQuery(id+"F2.wireOp",EDGE,"E7"),sQuery(id+"F2.wireOp",EDGE,"E8"),sQuery(id+"F2.wireOp",EDGE,"E10")])]}),"instanceName":"49"});
            var Q51;
            Q51=makeQuery(id+"F5.opPattern","COPY",BODY,{"derivedFrom":makeQuery(id+"F3.opExtrude","SWEPT_BODY",BODY,{"disambiguationData":[OSD([sQuery(id+"F2.wireOp",EDGE,"E2"),sQuery(id+"F2.wireOp",EDGE,"E3"),sQuery(id+"F2.wireOp",EDGE,"E4"),sQuery(id+"F2.wireOp",EDGE,"E5.filletArc"),sQuery(id+"F2.wireOp",EDGE,"E6.filletArc"),sQuery(id+"F2.wireOp",EDGE,"E7"),sQuery(id+"F2.wireOp",EDGE,"E8"),sQuery(id+"F2.wireOp",EDGE,"E10")])]}),"instanceName":"50"});
            var Q52;
            Q52=makeQuery(id+"F5.opPattern","COPY",BODY,{"derivedFrom":makeQuery(id+"F3.opExtrude","SWEPT_BODY",BODY,{"disambiguationData":[OSD([sQuery(id+"F2.wireOp",EDGE,"E2"),sQuery(id+"F2.wireOp",EDGE,"E3"),sQuery(id+"F2.wireOp",EDGE,"E4"),sQuery(id+"F2.wireOp",EDGE,"E5.filletArc"),sQuery(id+"F2.wireOp",EDGE,"E6.filletArc"),sQuery(id+"F2.wireOp",EDGE,"E7"),sQuery(id+"F2.wireOp",EDGE,"E8"),sQuery(id+"F2.wireOp",EDGE,"E10")])]}),"instanceName":"51"});
            var Q53;
            Q53=makeQuery(id+"F5.opPattern","COPY",BODY,{"derivedFrom":makeQuery(id+"F3.opExtrude","SWEPT_BODY",BODY,{"disambiguationData":[OSD([sQuery(id+"F2.wireOp",EDGE,"E2"),sQuery(id+"F2.wireOp",EDGE,"E3"),sQuery(id+"F2.wireOp",EDGE,"E4"),sQuery(id+"F2.wireOp",EDGE,"E5.filletArc"),sQuery(id+"F2.wireOp",EDGE,"E6.filletArc"),sQuery(id+"F2.wireOp",EDGE,"E7"),sQuery(id+"F2.wireOp",EDGE,"E8"),sQuery(id+"F2.wireOp",EDGE,"E10")])]}),"instanceName":"52"});
            var Q54;
            Q54=makeQuery(id+"F5.opPattern","COPY",BODY,{"derivedFrom":makeQuery(id+"F3.opExtrude","SWEPT_BODY",BODY,{"disambiguationData":[OSD([sQuery(id+"F2.wireOp",EDGE,"E2"),sQuery(id+"F2.wireOp",EDGE,"E3"),sQuery(id+"F2.wireOp",EDGE,"E4"),sQuery(id+"F2.wireOp",EDGE,"E5.filletArc"),sQuery(id+"F2.wireOp",EDGE,"E6.filletArc"),sQuery(id+"F2.wireOp",EDGE,"E7"),sQuery(id+"F2.wireOp",EDGE,"E8"),sQuery(id+"F2.wireOp",EDGE,"E10")])]}),"instanceName":"53"});
            var Q55;
            Q55=makeQuery(id+"F5.opPattern","COPY",BODY,{"derivedFrom":makeQuery(id+"F3.opExtrude","SWEPT_BODY",BODY,{"disambiguationData":[OSD([sQuery(id+"F2.wireOp",EDGE,"E2"),sQuery(id+"F2.wireOp",EDGE,"E3"),sQuery(id+"F2.wireOp",EDGE,"E4"),sQuery(id+"F2.wireOp",EDGE,"E5.filletArc"),sQuery(id+"F2.wireOp",EDGE,"E6.filletArc"),sQuery(id+"F2.wireOp",EDGE,"E7"),sQuery(id+"F2.wireOp",EDGE,"E8"),sQuery(id+"F2.wireOp",EDGE,"E10")])]}),"instanceName":"54"});
            var Q56;
            Q56=makeQuery(id+"F5.opPattern","COPY",BODY,{"derivedFrom":makeQuery(id+"F3.opExtrude","SWEPT_BODY",BODY,{"disambiguationData":[OSD([sQuery(id+"F2.wireOp",EDGE,"E2"),sQuery(id+"F2.wireOp",EDGE,"E3"),sQuery(id+"F2.wireOp",EDGE,"E4"),sQuery(id+"F2.wireOp",EDGE,"E5.filletArc"),sQuery(id+"F2.wireOp",EDGE,"E6.filletArc"),sQuery(id+"F2.wireOp",EDGE,"E7"),sQuery(id+"F2.wireOp",EDGE,"E8"),sQuery(id+"F2.wireOp",EDGE,"E10")])]}),"instanceName":"55"});
            var Q57;
            Q57=makeQuery(id+"F5.opPattern","COPY",BODY,{"derivedFrom":makeQuery(id+"F3.opExtrude","SWEPT_BODY",BODY,{"disambiguationData":[OSD([sQuery(id+"F2.wireOp",EDGE,"E2"),sQuery(id+"F2.wireOp",EDGE,"E3"),sQuery(id+"F2.wireOp",EDGE,"E4"),sQuery(id+"F2.wireOp",EDGE,"E5.filletArc"),sQuery(id+"F2.wireOp",EDGE,"E6.filletArc"),sQuery(id+"F2.wireOp",EDGE,"E7"),sQuery(id+"F2.wireOp",EDGE,"E8"),sQuery(id+"F2.wireOp",EDGE,"E10")])]}),"instanceName":"56"});
            var Q58;
            Q58=makeQuery(id+"F5.opPattern","COPY",BODY,{"derivedFrom":makeQuery(id+"F3.opExtrude","SWEPT_BODY",BODY,{"disambiguationData":[OSD([sQuery(id+"F2.wireOp",EDGE,"E2"),sQuery(id+"F2.wireOp",EDGE,"E3"),sQuery(id+"F2.wireOp",EDGE,"E4"),sQuery(id+"F2.wireOp",EDGE,"E5.filletArc"),sQuery(id+"F2.wireOp",EDGE,"E6.filletArc"),sQuery(id+"F2.wireOp",EDGE,"E7"),sQuery(id+"F2.wireOp",EDGE,"E8"),sQuery(id+"F2.wireOp",EDGE,"E10")])]}),"instanceName":"57"});
            var Q59;
            Q59=makeQuery(id+"F5.opPattern","COPY",BODY,{"derivedFrom":makeQuery(id+"F3.opExtrude","SWEPT_BODY",BODY,{"disambiguationData":[OSD([sQuery(id+"F2.wireOp",EDGE,"E2"),sQuery(id+"F2.wireOp",EDGE,"E3"),sQuery(id+"F2.wireOp",EDGE,"E4"),sQuery(id+"F2.wireOp",EDGE,"E5.filletArc"),sQuery(id+"F2.wireOp",EDGE,"E6.filletArc"),sQuery(id+"F2.wireOp",EDGE,"E7"),sQuery(id+"F2.wireOp",EDGE,"E8"),sQuery(id+"F2.wireOp",EDGE,"E10")])]}),"instanceName":"58"});
            var Q60;
            Q60=makeQuery(id+"F5.opPattern","COPY",BODY,{"derivedFrom":makeQuery(id+"F3.opExtrude","SWEPT_BODY",BODY,{"disambiguationData":[OSD([sQuery(id+"F2.wireOp",EDGE,"E2"),sQuery(id+"F2.wireOp",EDGE,"E3"),sQuery(id+"F2.wireOp",EDGE,"E4"),sQuery(id+"F2.wireOp",EDGE,"E5.filletArc"),sQuery(id+"F2.wireOp",EDGE,"E6.filletArc"),sQuery(id+"F2.wireOp",EDGE,"E7"),sQuery(id+"F2.wireOp",EDGE,"E8"),sQuery(id+"F2.wireOp",EDGE,"E10")])]}),"instanceName":"59"});
            var Q61;
            Q61=makeQuery(id+"F5.opPattern","COPY",BODY,{"derivedFrom":makeQuery(id+"F3.opExtrude","SWEPT_BODY",BODY,{"disambiguationData":[OSD([sQuery(id+"F2.wireOp",EDGE,"E2"),sQuery(id+"F2.wireOp",EDGE,"E3"),sQuery(id+"F2.wireOp",EDGE,"E4"),sQuery(id+"F2.wireOp",EDGE,"E5.filletArc"),sQuery(id+"F2.wireOp",EDGE,"E6.filletArc"),sQuery(id+"F2.wireOp",EDGE,"E7"),sQuery(id+"F2.wireOp",EDGE,"E8"),sQuery(id+"F2.wireOp",EDGE,"E10")])]}),"instanceName":"60"});
            var Q62;
            Q62=makeQuery(id+"F5.opPattern","COPY",BODY,{"derivedFrom":makeQuery(id+"F3.opExtrude","SWEPT_BODY",BODY,{"disambiguationData":[OSD([sQuery(id+"F2.wireOp",EDGE,"E2"),sQuery(id+"F2.wireOp",EDGE,"E3"),sQuery(id+"F2.wireOp",EDGE,"E4"),sQuery(id+"F2.wireOp",EDGE,"E5.filletArc"),sQuery(id+"F2.wireOp",EDGE,"E6.filletArc"),sQuery(id+"F2.wireOp",EDGE,"E7"),sQuery(id+"F2.wireOp",EDGE,"E8"),sQuery(id+"F2.wireOp",EDGE,"E10")])]}),"instanceName":"61"});
            var Q63;
            Q63=makeQuery(id+"F5.opPattern","COPY",BODY,{"derivedFrom":makeQuery(id+"F3.opExtrude","SWEPT_BODY",BODY,{"disambiguationData":[OSD([sQuery(id+"F2.wireOp",EDGE,"E2"),sQuery(id+"F2.wireOp",EDGE,"E3"),sQuery(id+"F2.wireOp",EDGE,"E4"),sQuery(id+"F2.wireOp",EDGE,"E5.filletArc"),sQuery(id+"F2.wireOp",EDGE,"E6.filletArc"),sQuery(id+"F2.wireOp",EDGE,"E7"),sQuery(id+"F2.wireOp",EDGE,"E8"),sQuery(id+"F2.wireOp",EDGE,"E10")])]}),"instanceName":"62"});
            var Q64;
            Q64=makeQuery(id+"F5.opPattern","COPY",BODY,{"derivedFrom":makeQuery(id+"F3.opExtrude","SWEPT_BODY",BODY,{"disambiguationData":[OSD([sQuery(id+"F2.wireOp",EDGE,"E2"),sQuery(id+"F2.wireOp",EDGE,"E3"),sQuery(id+"F2.wireOp",EDGE,"E4"),sQuery(id+"F2.wireOp",EDGE,"E5.filletArc"),sQuery(id+"F2.wireOp",EDGE,"E6.filletArc"),sQuery(id+"F2.wireOp",EDGE,"E7"),sQuery(id+"F2.wireOp",EDGE,"E8"),sQuery(id+"F2.wireOp",EDGE,"E10")])]}),"instanceName":"63"});
            var Q65;
            Q65=makeQuery(id+"F5.opPattern","COPY",BODY,{"derivedFrom":makeQuery(id+"F3.opExtrude","SWEPT_BODY",BODY,{"disambiguationData":[OSD([sQuery(id+"F2.wireOp",EDGE,"E2"),sQuery(id+"F2.wireOp",EDGE,"E3"),sQuery(id+"F2.wireOp",EDGE,"E4"),sQuery(id+"F2.wireOp",EDGE,"E5.filletArc"),sQuery(id+"F2.wireOp",EDGE,"E6.filletArc"),sQuery(id+"F2.wireOp",EDGE,"E7"),sQuery(id+"F2.wireOp",EDGE,"E8"),sQuery(id+"F2.wireOp",EDGE,"E10")])]}),"instanceName":"64"});
            var Q66;
            Q66=makeQuery(id+"F5.opPattern","COPY",BODY,{"derivedFrom":makeQuery(id+"F3.opExtrude","SWEPT_BODY",BODY,{"disambiguationData":[OSD([sQuery(id+"F2.wireOp",EDGE,"E2"),sQuery(id+"F2.wireOp",EDGE,"E3"),sQuery(id+"F2.wireOp",EDGE,"E4"),sQuery(id+"F2.wireOp",EDGE,"E5.filletArc"),sQuery(id+"F2.wireOp",EDGE,"E6.filletArc"),sQuery(id+"F2.wireOp",EDGE,"E7"),sQuery(id+"F2.wireOp",EDGE,"E8"),sQuery(id+"F2.wireOp",EDGE,"E10")])]}),"instanceName":"65"});
            var Q67;
            Q67=makeQuery(id+"F5.opPattern","COPY",BODY,{"derivedFrom":makeQuery(id+"F3.opExtrude","SWEPT_BODY",BODY,{"disambiguationData":[OSD([sQuery(id+"F2.wireOp",EDGE,"E2"),sQuery(id+"F2.wireOp",EDGE,"E3"),sQuery(id+"F2.wireOp",EDGE,"E4"),sQuery(id+"F2.wireOp",EDGE,"E5.filletArc"),sQuery(id+"F2.wireOp",EDGE,"E6.filletArc"),sQuery(id+"F2.wireOp",EDGE,"E7"),sQuery(id+"F2.wireOp",EDGE,"E8"),sQuery(id+"F2.wireOp",EDGE,"E10")])]}),"instanceName":"66"});
            var Q68;
            Q68=makeQuery(id+"F5.opPattern","COPY",BODY,{"derivedFrom":makeQuery(id+"F3.opExtrude","SWEPT_BODY",BODY,{"disambiguationData":[OSD([sQuery(id+"F2.wireOp",EDGE,"E2"),sQuery(id+"F2.wireOp",EDGE,"E3"),sQuery(id+"F2.wireOp",EDGE,"E4"),sQuery(id+"F2.wireOp",EDGE,"E5.filletArc"),sQuery(id+"F2.wireOp",EDGE,"E6.filletArc"),sQuery(id+"F2.wireOp",EDGE,"E7"),sQuery(id+"F2.wireOp",EDGE,"E8"),sQuery(id+"F2.wireOp",EDGE,"E10")])]}),"instanceName":"67"});
            var Q69;
            Q69=makeQuery(id+"F5.opPattern","COPY",BODY,{"derivedFrom":makeQuery(id+"F3.opExtrude","SWEPT_BODY",BODY,{"disambiguationData":[OSD([sQuery(id+"F2.wireOp",EDGE,"E2"),sQuery(id+"F2.wireOp",EDGE,"E3"),sQuery(id+"F2.wireOp",EDGE,"E4"),sQuery(id+"F2.wireOp",EDGE,"E5.filletArc"),sQuery(id+"F2.wireOp",EDGE,"E6.filletArc"),sQuery(id+"F2.wireOp",EDGE,"E7"),sQuery(id+"F2.wireOp",EDGE,"E8"),sQuery(id+"F2.wireOp",EDGE,"E10")])]}),"instanceName":"68"});
            var Q70;
            Q70=makeQuery(id+"F5.opPattern","COPY",BODY,{"derivedFrom":makeQuery(id+"F3.opExtrude","SWEPT_BODY",BODY,{"disambiguationData":[OSD([sQuery(id+"F2.wireOp",EDGE,"E2"),sQuery(id+"F2.wireOp",EDGE,"E3"),sQuery(id+"F2.wireOp",EDGE,"E4"),sQuery(id+"F2.wireOp",EDGE,"E5.filletArc"),sQuery(id+"F2.wireOp",EDGE,"E6.filletArc"),sQuery(id+"F2.wireOp",EDGE,"E7"),sQuery(id+"F2.wireOp",EDGE,"E8"),sQuery(id+"F2.wireOp",EDGE,"E10")])]}),"instanceName":"69"});
            var Q71;
            Q71=makeQuery(id+"F5.opPattern","COPY",BODY,{"derivedFrom":makeQuery(id+"F3.opExtrude","SWEPT_BODY",BODY,{"disambiguationData":[OSD([sQuery(id+"F2.wireOp",EDGE,"E2"),sQuery(id+"F2.wireOp",EDGE,"E3"),sQuery(id+"F2.wireOp",EDGE,"E4"),sQuery(id+"F2.wireOp",EDGE,"E5.filletArc"),sQuery(id+"F2.wireOp",EDGE,"E6.filletArc"),sQuery(id+"F2.wireOp",EDGE,"E7"),sQuery(id+"F2.wireOp",EDGE,"E8"),sQuery(id+"F2.wireOp",EDGE,"E10")])]}),"instanceName":"70"});
            var Q72;
            Q72=makeQuery(id+"F5.opPattern","COPY",BODY,{"derivedFrom":makeQuery(id+"F3.opExtrude","SWEPT_BODY",BODY,{"disambiguationData":[OSD([sQuery(id+"F2.wireOp",EDGE,"E2"),sQuery(id+"F2.wireOp",EDGE,"E3"),sQuery(id+"F2.wireOp",EDGE,"E4"),sQuery(id+"F2.wireOp",EDGE,"E5.filletArc"),sQuery(id+"F2.wireOp",EDGE,"E6.filletArc"),sQuery(id+"F2.wireOp",EDGE,"E7"),sQuery(id+"F2.wireOp",EDGE,"E8"),sQuery(id+"F2.wireOp",EDGE,"E10")])]}),"instanceName":"71"});
            var Q73;
            Q73=makeQuery(id+"F5.opPattern","COPY",BODY,{"derivedFrom":makeQuery(id+"F3.opExtrude","SWEPT_BODY",BODY,{"disambiguationData":[OSD([sQuery(id+"F2.wireOp",EDGE,"E2"),sQuery(id+"F2.wireOp",EDGE,"E3"),sQuery(id+"F2.wireOp",EDGE,"E4"),sQuery(id+"F2.wireOp",EDGE,"E5.filletArc"),sQuery(id+"F2.wireOp",EDGE,"E6.filletArc"),sQuery(id+"F2.wireOp",EDGE,"E7"),sQuery(id+"F2.wireOp",EDGE,"E8"),sQuery(id+"F2.wireOp",EDGE,"E10")])]}),"instanceName":"72"});
            var Q74;
            Q74=makeQuery(id+"F5.opPattern","COPY",BODY,{"derivedFrom":makeQuery(id+"F3.opExtrude","SWEPT_BODY",BODY,{"disambiguationData":[OSD([sQuery(id+"F2.wireOp",EDGE,"E2"),sQuery(id+"F2.wireOp",EDGE,"E3"),sQuery(id+"F2.wireOp",EDGE,"E4"),sQuery(id+"F2.wireOp",EDGE,"E5.filletArc"),sQuery(id+"F2.wireOp",EDGE,"E6.filletArc"),sQuery(id+"F2.wireOp",EDGE,"E7"),sQuery(id+"F2.wireOp",EDGE,"E8"),sQuery(id+"F2.wireOp",EDGE,"E10")])]}),"instanceName":"73"});
            var Q75;
            Q75=makeQuery(id+"F5.opPattern","COPY",BODY,{"derivedFrom":makeQuery(id+"F3.opExtrude","SWEPT_BODY",BODY,{"disambiguationData":[OSD([sQuery(id+"F2.wireOp",EDGE,"E2"),sQuery(id+"F2.wireOp",EDGE,"E3"),sQuery(id+"F2.wireOp",EDGE,"E4"),sQuery(id+"F2.wireOp",EDGE,"E5.filletArc"),sQuery(id+"F2.wireOp",EDGE,"E6.filletArc"),sQuery(id+"F2.wireOp",EDGE,"E7"),sQuery(id+"F2.wireOp",EDGE,"E8"),sQuery(id+"F2.wireOp",EDGE,"E10")])]}),"instanceName":"74"});
            var Q76;
            Q76=makeQuery(id+"F5.opPattern","COPY",BODY,{"derivedFrom":makeQuery(id+"F3.opExtrude","SWEPT_BODY",BODY,{"disambiguationData":[OSD([sQuery(id+"F2.wireOp",EDGE,"E2"),sQuery(id+"F2.wireOp",EDGE,"E3"),sQuery(id+"F2.wireOp",EDGE,"E4"),sQuery(id+"F2.wireOp",EDGE,"E5.filletArc"),sQuery(id+"F2.wireOp",EDGE,"E6.filletArc"),sQuery(id+"F2.wireOp",EDGE,"E7"),sQuery(id+"F2.wireOp",EDGE,"E8"),sQuery(id+"F2.wireOp",EDGE,"E10")])]}),"instanceName":"75"});
            var Q77;
            Q77=makeQuery(id+"F5.opPattern","COPY",BODY,{"derivedFrom":makeQuery(id+"F3.opExtrude","SWEPT_BODY",BODY,{"disambiguationData":[OSD([sQuery(id+"F2.wireOp",EDGE,"E2"),sQuery(id+"F2.wireOp",EDGE,"E3"),sQuery(id+"F2.wireOp",EDGE,"E4"),sQuery(id+"F2.wireOp",EDGE,"E5.filletArc"),sQuery(id+"F2.wireOp",EDGE,"E6.filletArc"),sQuery(id+"F2.wireOp",EDGE,"E7"),sQuery(id+"F2.wireOp",EDGE,"E8"),sQuery(id+"F2.wireOp",EDGE,"E10")])]}),"instanceName":"76"});
            var Q78;
            Q78=makeQuery(id+"F5.opPattern","COPY",BODY,{"derivedFrom":makeQuery(id+"F3.opExtrude","SWEPT_BODY",BODY,{"disambiguationData":[OSD([sQuery(id+"F2.wireOp",EDGE,"E2"),sQuery(id+"F2.wireOp",EDGE,"E3"),sQuery(id+"F2.wireOp",EDGE,"E4"),sQuery(id+"F2.wireOp",EDGE,"E5.filletArc"),sQuery(id+"F2.wireOp",EDGE,"E6.filletArc"),sQuery(id+"F2.wireOp",EDGE,"E7"),sQuery(id+"F2.wireOp",EDGE,"E8"),sQuery(id+"F2.wireOp",EDGE,"E10")])]}),"instanceName":"77"});
            var Q79;
            Q79=makeQuery(id+"F5.opPattern","COPY",BODY,{"derivedFrom":makeQuery(id+"F3.opExtrude","SWEPT_BODY",BODY,{"disambiguationData":[OSD([sQuery(id+"F2.wireOp",EDGE,"E2"),sQuery(id+"F2.wireOp",EDGE,"E3"),sQuery(id+"F2.wireOp",EDGE,"E4"),sQuery(id+"F2.wireOp",EDGE,"E5.filletArc"),sQuery(id+"F2.wireOp",EDGE,"E6.filletArc"),sQuery(id+"F2.wireOp",EDGE,"E7"),sQuery(id+"F2.wireOp",EDGE,"E8"),sQuery(id+"F2.wireOp",EDGE,"E10")])]}),"instanceName":"78"});
            var Q80;
            Q80=makeQuery(id+"F5.opPattern","COPY",BODY,{"derivedFrom":makeQuery(id+"F3.opExtrude","SWEPT_BODY",BODY,{"disambiguationData":[OSD([sQuery(id+"F2.wireOp",EDGE,"E2"),sQuery(id+"F2.wireOp",EDGE,"E3"),sQuery(id+"F2.wireOp",EDGE,"E4"),sQuery(id+"F2.wireOp",EDGE,"E5.filletArc"),sQuery(id+"F2.wireOp",EDGE,"E6.filletArc"),sQuery(id+"F2.wireOp",EDGE,"E7"),sQuery(id+"F2.wireOp",EDGE,"E8"),sQuery(id+"F2.wireOp",EDGE,"E10")])]}),"instanceName":"79"});
            var Q81;
            Q81=makeQuery(id+"F5.opPattern","COPY",BODY,{"derivedFrom":makeQuery(id+"F3.opExtrude","SWEPT_BODY",BODY,{"disambiguationData":[OSD([sQuery(id+"F2.wireOp",EDGE,"E2"),sQuery(id+"F2.wireOp",EDGE,"E3"),sQuery(id+"F2.wireOp",EDGE,"E4"),sQuery(id+"F2.wireOp",EDGE,"E5.filletArc"),sQuery(id+"F2.wireOp",EDGE,"E6.filletArc"),sQuery(id+"F2.wireOp",EDGE,"E7"),sQuery(id+"F2.wireOp",EDGE,"E8"),sQuery(id+"F2.wireOp",EDGE,"E10")])]}),"instanceName":"80"});
            var Q82;
            Q82=makeQuery(id+"F5.opPattern","COPY",BODY,{"derivedFrom":makeQuery(id+"F3.opExtrude","SWEPT_BODY",BODY,{"disambiguationData":[OSD([sQuery(id+"F2.wireOp",EDGE,"E2"),sQuery(id+"F2.wireOp",EDGE,"E3"),sQuery(id+"F2.wireOp",EDGE,"E4"),sQuery(id+"F2.wireOp",EDGE,"E5.filletArc"),sQuery(id+"F2.wireOp",EDGE,"E6.filletArc"),sQuery(id+"F2.wireOp",EDGE,"E7"),sQuery(id+"F2.wireOp",EDGE,"E8"),sQuery(id+"F2.wireOp",EDGE,"E10")])]}),"instanceName":"81"});
            var Q83;
            Q83=makeQuery(id+"F5.opPattern","COPY",BODY,{"derivedFrom":makeQuery(id+"F3.opExtrude","SWEPT_BODY",BODY,{"disambiguationData":[OSD([sQuery(id+"F2.wireOp",EDGE,"E2"),sQuery(id+"F2.wireOp",EDGE,"E3"),sQuery(id+"F2.wireOp",EDGE,"E4"),sQuery(id+"F2.wireOp",EDGE,"E5.filletArc"),sQuery(id+"F2.wireOp",EDGE,"E6.filletArc"),sQuery(id+"F2.wireOp",EDGE,"E7"),sQuery(id+"F2.wireOp",EDGE,"E8"),sQuery(id+"F2.wireOp",EDGE,"E10")])]}),"instanceName":"82"});
            var Q84;
            Q84=makeQuery(id+"F5.opPattern","COPY",BODY,{"derivedFrom":makeQuery(id+"F3.opExtrude","SWEPT_BODY",BODY,{"disambiguationData":[OSD([sQuery(id+"F2.wireOp",EDGE,"E2"),sQuery(id+"F2.wireOp",EDGE,"E3"),sQuery(id+"F2.wireOp",EDGE,"E4"),sQuery(id+"F2.wireOp",EDGE,"E5.filletArc"),sQuery(id+"F2.wireOp",EDGE,"E6.filletArc"),sQuery(id+"F2.wireOp",EDGE,"E7"),sQuery(id+"F2.wireOp",EDGE,"E8"),sQuery(id+"F2.wireOp",EDGE,"E10")])]}),"instanceName":"83"});
            var Q85;
            Q85=makeQuery(id+"F5.opPattern","COPY",BODY,{"derivedFrom":makeQuery(id+"F3.opExtrude","SWEPT_BODY",BODY,{"disambiguationData":[OSD([sQuery(id+"F2.wireOp",EDGE,"E2"),sQuery(id+"F2.wireOp",EDGE,"E3"),sQuery(id+"F2.wireOp",EDGE,"E4"),sQuery(id+"F2.wireOp",EDGE,"E5.filletArc"),sQuery(id+"F2.wireOp",EDGE,"E6.filletArc"),sQuery(id+"F2.wireOp",EDGE,"E7"),sQuery(id+"F2.wireOp",EDGE,"E8"),sQuery(id+"F2.wireOp",EDGE,"E10")])]}),"instanceName":"84"});
            var Q86;
            Q86=makeQuery(id+"F5.opPattern","COPY",BODY,{"derivedFrom":makeQuery(id+"F3.opExtrude","SWEPT_BODY",BODY,{"disambiguationData":[OSD([sQuery(id+"F2.wireOp",EDGE,"E2"),sQuery(id+"F2.wireOp",EDGE,"E3"),sQuery(id+"F2.wireOp",EDGE,"E4"),sQuery(id+"F2.wireOp",EDGE,"E5.filletArc"),sQuery(id+"F2.wireOp",EDGE,"E6.filletArc"),sQuery(id+"F2.wireOp",EDGE,"E7"),sQuery(id+"F2.wireOp",EDGE,"E8"),sQuery(id+"F2.wireOp",EDGE,"E10")])]}),"instanceName":"85"});
            var Q87;
            Q87=makeQuery(id+"F5.opPattern","COPY",BODY,{"derivedFrom":makeQuery(id+"F3.opExtrude","SWEPT_BODY",BODY,{"disambiguationData":[OSD([sQuery(id+"F2.wireOp",EDGE,"E2"),sQuery(id+"F2.wireOp",EDGE,"E3"),sQuery(id+"F2.wireOp",EDGE,"E4"),sQuery(id+"F2.wireOp",EDGE,"E5.filletArc"),sQuery(id+"F2.wireOp",EDGE,"E6.filletArc"),sQuery(id+"F2.wireOp",EDGE,"E7"),sQuery(id+"F2.wireOp",EDGE,"E8"),sQuery(id+"F2.wireOp",EDGE,"E10")])]}),"instanceName":"86"});
            var Q88;
            Q88=makeQuery(id+"F5.opPattern","COPY",BODY,{"derivedFrom":makeQuery(id+"F3.opExtrude","SWEPT_BODY",BODY,{"disambiguationData":[OSD([sQuery(id+"F2.wireOp",EDGE,"E2"),sQuery(id+"F2.wireOp",EDGE,"E3"),sQuery(id+"F2.wireOp",EDGE,"E4"),sQuery(id+"F2.wireOp",EDGE,"E5.filletArc"),sQuery(id+"F2.wireOp",EDGE,"E6.filletArc"),sQuery(id+"F2.wireOp",EDGE,"E7"),sQuery(id+"F2.wireOp",EDGE,"E8"),sQuery(id+"F2.wireOp",EDGE,"E10")])]}),"instanceName":"87"});
            var Q89;
            Q89=makeQuery(id+"F5.opPattern","COPY",BODY,{"derivedFrom":makeQuery(id+"F3.opExtrude","SWEPT_BODY",BODY,{"disambiguationData":[OSD([sQuery(id+"F2.wireOp",EDGE,"E2"),sQuery(id+"F2.wireOp",EDGE,"E3"),sQuery(id+"F2.wireOp",EDGE,"E4"),sQuery(id+"F2.wireOp",EDGE,"E5.filletArc"),sQuery(id+"F2.wireOp",EDGE,"E6.filletArc"),sQuery(id+"F2.wireOp",EDGE,"E7"),sQuery(id+"F2.wireOp",EDGE,"E8"),sQuery(id+"F2.wireOp",EDGE,"E10")])]}),"instanceName":"88"});
            var Q90;
            Q90=makeQuery(id+"F5.opPattern","COPY",BODY,{"derivedFrom":makeQuery(id+"F3.opExtrude","SWEPT_BODY",BODY,{"disambiguationData":[OSD([sQuery(id+"F2.wireOp",EDGE,"E2"),sQuery(id+"F2.wireOp",EDGE,"E3"),sQuery(id+"F2.wireOp",EDGE,"E4"),sQuery(id+"F2.wireOp",EDGE,"E5.filletArc"),sQuery(id+"F2.wireOp",EDGE,"E6.filletArc"),sQuery(id+"F2.wireOp",EDGE,"E7"),sQuery(id+"F2.wireOp",EDGE,"E8"),sQuery(id+"F2.wireOp",EDGE,"E10")])]}),"instanceName":"89"});
            var Q91;
            Q91=makeQuery(id+"F5.opPattern","COPY",BODY,{"derivedFrom":makeQuery(id+"F3.opExtrude","SWEPT_BODY",BODY,{"disambiguationData":[OSD([sQuery(id+"F2.wireOp",EDGE,"E2"),sQuery(id+"F2.wireOp",EDGE,"E3"),sQuery(id+"F2.wireOp",EDGE,"E4"),sQuery(id+"F2.wireOp",EDGE,"E5.filletArc"),sQuery(id+"F2.wireOp",EDGE,"E6.filletArc"),sQuery(id+"F2.wireOp",EDGE,"E7"),sQuery(id+"F2.wireOp",EDGE,"E8"),sQuery(id+"F2.wireOp",EDGE,"E10")])]}),"instanceName":"90"});
            var Q92;
            Q92=makeQuery(id+"F5.opPattern","COPY",BODY,{"derivedFrom":makeQuery(id+"F3.opExtrude","SWEPT_BODY",BODY,{"disambiguationData":[OSD([sQuery(id+"F2.wireOp",EDGE,"E2"),sQuery(id+"F2.wireOp",EDGE,"E3"),sQuery(id+"F2.wireOp",EDGE,"E4"),sQuery(id+"F2.wireOp",EDGE,"E5.filletArc"),sQuery(id+"F2.wireOp",EDGE,"E6.filletArc"),sQuery(id+"F2.wireOp",EDGE,"E7"),sQuery(id+"F2.wireOp",EDGE,"E8"),sQuery(id+"F2.wireOp",EDGE,"E10")])]}),"instanceName":"91"});
            var Q93;
            Q93=makeQuery(id+"F5.opPattern","COPY",BODY,{"derivedFrom":makeQuery(id+"F3.opExtrude","SWEPT_BODY",BODY,{"disambiguationData":[OSD([sQuery(id+"F2.wireOp",EDGE,"E2"),sQuery(id+"F2.wireOp",EDGE,"E3"),sQuery(id+"F2.wireOp",EDGE,"E4"),sQuery(id+"F2.wireOp",EDGE,"E5.filletArc"),sQuery(id+"F2.wireOp",EDGE,"E6.filletArc"),sQuery(id+"F2.wireOp",EDGE,"E7"),sQuery(id+"F2.wireOp",EDGE,"E8"),sQuery(id+"F2.wireOp",EDGE,"E10")])]}),"instanceName":"92"});
            var Q94;
            Q94=makeQuery(id+"F5.opPattern","COPY",BODY,{"derivedFrom":makeQuery(id+"F3.opExtrude","SWEPT_BODY",BODY,{"disambiguationData":[OSD([sQuery(id+"F2.wireOp",EDGE,"E2"),sQuery(id+"F2.wireOp",EDGE,"E3"),sQuery(id+"F2.wireOp",EDGE,"E4"),sQuery(id+"F2.wireOp",EDGE,"E5.filletArc"),sQuery(id+"F2.wireOp",EDGE,"E6.filletArc"),sQuery(id+"F2.wireOp",EDGE,"E7"),sQuery(id+"F2.wireOp",EDGE,"E8"),sQuery(id+"F2.wireOp",EDGE,"E10")])]}),"instanceName":"93"});
            var Q95;
            Q95=makeQuery(id+"F5.opPattern","COPY",BODY,{"derivedFrom":makeQuery(id+"F3.opExtrude","SWEPT_BODY",BODY,{"disambiguationData":[OSD([sQuery(id+"F2.wireOp",EDGE,"E2"),sQuery(id+"F2.wireOp",EDGE,"E3"),sQuery(id+"F2.wireOp",EDGE,"E4"),sQuery(id+"F2.wireOp",EDGE,"E5.filletArc"),sQuery(id+"F2.wireOp",EDGE,"E6.filletArc"),sQuery(id+"F2.wireOp",EDGE,"E7"),sQuery(id+"F2.wireOp",EDGE,"E8"),sQuery(id+"F2.wireOp",EDGE,"E10")])]}),"instanceName":"94"});
            var Q96;
            Q96=makeQuery(id+"F5.opPattern","COPY",BODY,{"derivedFrom":makeQuery(id+"F3.opExtrude","SWEPT_BODY",BODY,{"disambiguationData":[OSD([sQuery(id+"F2.wireOp",EDGE,"E2"),sQuery(id+"F2.wireOp",EDGE,"E3"),sQuery(id+"F2.wireOp",EDGE,"E4"),sQuery(id+"F2.wireOp",EDGE,"E5.filletArc"),sQuery(id+"F2.wireOp",EDGE,"E6.filletArc"),sQuery(id+"F2.wireOp",EDGE,"E7"),sQuery(id+"F2.wireOp",EDGE,"E8"),sQuery(id+"F2.wireOp",EDGE,"E10")])]}),"instanceName":"95"});
            var Q97;
            Q97=makeQuery(id+"F5.opPattern","COPY",BODY,{"derivedFrom":makeQuery(id+"F3.opExtrude","SWEPT_BODY",BODY,{"disambiguationData":[OSD([sQuery(id+"F2.wireOp",EDGE,"E2"),sQuery(id+"F2.wireOp",EDGE,"E3"),sQuery(id+"F2.wireOp",EDGE,"E4"),sQuery(id+"F2.wireOp",EDGE,"E5.filletArc"),sQuery(id+"F2.wireOp",EDGE,"E6.filletArc"),sQuery(id+"F2.wireOp",EDGE,"E7"),sQuery(id+"F2.wireOp",EDGE,"E8"),sQuery(id+"F2.wireOp",EDGE,"E10")])]}),"instanceName":"96"});
            var Q98;
            Q98=makeQuery(id+"F5.opPattern","COPY",BODY,{"derivedFrom":makeQuery(id+"F3.opExtrude","SWEPT_BODY",BODY,{"disambiguationData":[OSD([sQuery(id+"F2.wireOp",EDGE,"E2"),sQuery(id+"F2.wireOp",EDGE,"E3"),sQuery(id+"F2.wireOp",EDGE,"E4"),sQuery(id+"F2.wireOp",EDGE,"E5.filletArc"),sQuery(id+"F2.wireOp",EDGE,"E6.filletArc"),sQuery(id+"F2.wireOp",EDGE,"E7"),sQuery(id+"F2.wireOp",EDGE,"E8"),sQuery(id+"F2.wireOp",EDGE,"E10")])]}),"instanceName":"97"});
            var Q99;
            Q99=makeQuery(id+"F5.opPattern","COPY",BODY,{"derivedFrom":makeQuery(id+"F3.opExtrude","SWEPT_BODY",BODY,{"disambiguationData":[OSD([sQuery(id+"F2.wireOp",EDGE,"E2"),sQuery(id+"F2.wireOp",EDGE,"E3"),sQuery(id+"F2.wireOp",EDGE,"E4"),sQuery(id+"F2.wireOp",EDGE,"E5.filletArc"),sQuery(id+"F2.wireOp",EDGE,"E6.filletArc"),sQuery(id+"F2.wireOp",EDGE,"E7"),sQuery(id+"F2.wireOp",EDGE,"E8"),sQuery(id+"F2.wireOp",EDGE,"E10")])]}),"instanceName":"98"});
            var Q100;
            Q100=makeQuery(id+"F5.opPattern","COPY",BODY,{"derivedFrom":makeQuery(id+"F3.opExtrude","SWEPT_BODY",BODY,{"disambiguationData":[OSD([sQuery(id+"F2.wireOp",EDGE,"E2"),sQuery(id+"F2.wireOp",EDGE,"E3"),sQuery(id+"F2.wireOp",EDGE,"E4"),sQuery(id+"F2.wireOp",EDGE,"E5.filletArc"),sQuery(id+"F2.wireOp",EDGE,"E6.filletArc"),sQuery(id+"F2.wireOp",EDGE,"E7"),sQuery(id+"F2.wireOp",EDGE,"E8"),sQuery(id+"F2.wireOp",EDGE,"E10")])]}),"instanceName":"99"});
            var Q101;
            Q101=makeQuery(id+"F5.opPattern","COPY",BODY,{"derivedFrom":makeQuery(id+"F3.opExtrude","SWEPT_BODY",BODY,{"disambiguationData":[OSD([sQuery(id+"F2.wireOp",EDGE,"E2"),sQuery(id+"F2.wireOp",EDGE,"E3"),sQuery(id+"F2.wireOp",EDGE,"E4"),sQuery(id+"F2.wireOp",EDGE,"E5.filletArc"),sQuery(id+"F2.wireOp",EDGE,"E6.filletArc"),sQuery(id+"F2.wireOp",EDGE,"E7"),sQuery(id+"F2.wireOp",EDGE,"E8"),sQuery(id+"F2.wireOp",EDGE,"E10")])]}),"instanceName":"100"});
            var Q102;
            Q102=makeQuery(id+"F5.opPattern","COPY",BODY,{"derivedFrom":makeQuery(id+"F3.opExtrude","SWEPT_BODY",BODY,{"disambiguationData":[OSD([sQuery(id+"F2.wireOp",EDGE,"E2"),sQuery(id+"F2.wireOp",EDGE,"E3"),sQuery(id+"F2.wireOp",EDGE,"E4"),sQuery(id+"F2.wireOp",EDGE,"E5.filletArc"),sQuery(id+"F2.wireOp",EDGE,"E6.filletArc"),sQuery(id+"F2.wireOp",EDGE,"E7"),sQuery(id+"F2.wireOp",EDGE,"E8"),sQuery(id+"F2.wireOp",EDGE,"E10")])]}),"instanceName":"101"});
            var Q103;
            Q103=makeQuery(id+"F5.opPattern","COPY",BODY,{"derivedFrom":makeQuery(id+"F3.opExtrude","SWEPT_BODY",BODY,{"disambiguationData":[OSD([sQuery(id+"F2.wireOp",EDGE,"E2"),sQuery(id+"F2.wireOp",EDGE,"E3"),sQuery(id+"F2.wireOp",EDGE,"E4"),sQuery(id+"F2.wireOp",EDGE,"E5.filletArc"),sQuery(id+"F2.wireOp",EDGE,"E6.filletArc"),sQuery(id+"F2.wireOp",EDGE,"E7"),sQuery(id+"F2.wireOp",EDGE,"E8"),sQuery(id+"F2.wireOp",EDGE,"E10")])]}),"instanceName":"102"});
            var Q104;
            Q104=makeQuery(id+"F5.opPattern","COPY",BODY,{"derivedFrom":makeQuery(id+"F3.opExtrude","SWEPT_BODY",BODY,{"disambiguationData":[OSD([sQuery(id+"F2.wireOp",EDGE,"E2"),sQuery(id+"F2.wireOp",EDGE,"E3"),sQuery(id+"F2.wireOp",EDGE,"E4"),sQuery(id+"F2.wireOp",EDGE,"E5.filletArc"),sQuery(id+"F2.wireOp",EDGE,"E6.filletArc"),sQuery(id+"F2.wireOp",EDGE,"E7"),sQuery(id+"F2.wireOp",EDGE,"E8"),sQuery(id+"F2.wireOp",EDGE,"E10")])]}),"instanceName":"103"});
            var Q105;
            Q105=makeQuery(id+"F5.opPattern","COPY",BODY,{"derivedFrom":makeQuery(id+"F3.opExtrude","SWEPT_BODY",BODY,{"disambiguationData":[OSD([sQuery(id+"F2.wireOp",EDGE,"E2"),sQuery(id+"F2.wireOp",EDGE,"E3"),sQuery(id+"F2.wireOp",EDGE,"E4"),sQuery(id+"F2.wireOp",EDGE,"E5.filletArc"),sQuery(id+"F2.wireOp",EDGE,"E6.filletArc"),sQuery(id+"F2.wireOp",EDGE,"E7"),sQuery(id+"F2.wireOp",EDGE,"E8"),sQuery(id+"F2.wireOp",EDGE,"E10")])]}),"instanceName":"104"});
            var Q106;
            Q106=makeQuery(id+"F5.opPattern","COPY",BODY,{"derivedFrom":makeQuery(id+"F3.opExtrude","SWEPT_BODY",BODY,{"disambiguationData":[OSD([sQuery(id+"F2.wireOp",EDGE,"E2"),sQuery(id+"F2.wireOp",EDGE,"E3"),sQuery(id+"F2.wireOp",EDGE,"E4"),sQuery(id+"F2.wireOp",EDGE,"E5.filletArc"),sQuery(id+"F2.wireOp",EDGE,"E6.filletArc"),sQuery(id+"F2.wireOp",EDGE,"E7"),sQuery(id+"F2.wireOp",EDGE,"E8"),sQuery(id+"F2.wireOp",EDGE,"E10")])]}),"instanceName":"105"});
            var Q107;
            Q107=makeQuery(id+"F5.opPattern","COPY",BODY,{"derivedFrom":makeQuery(id+"F3.opExtrude","SWEPT_BODY",BODY,{"disambiguationData":[OSD([sQuery(id+"F2.wireOp",EDGE,"E2"),sQuery(id+"F2.wireOp",EDGE,"E3"),sQuery(id+"F2.wireOp",EDGE,"E4"),sQuery(id+"F2.wireOp",EDGE,"E5.filletArc"),sQuery(id+"F2.wireOp",EDGE,"E6.filletArc"),sQuery(id+"F2.wireOp",EDGE,"E7"),sQuery(id+"F2.wireOp",EDGE,"E8"),sQuery(id+"F2.wireOp",EDGE,"E10")])]}),"instanceName":"106"});
            var Q108;
            Q108=makeQuery(id+"F5.opPattern","COPY",BODY,{"derivedFrom":makeQuery(id+"F3.opExtrude","SWEPT_BODY",BODY,{"disambiguationData":[OSD([sQuery(id+"F2.wireOp",EDGE,"E2"),sQuery(id+"F2.wireOp",EDGE,"E3"),sQuery(id+"F2.wireOp",EDGE,"E4"),sQuery(id+"F2.wireOp",EDGE,"E5.filletArc"),sQuery(id+"F2.wireOp",EDGE,"E6.filletArc"),sQuery(id+"F2.wireOp",EDGE,"E7"),sQuery(id+"F2.wireOp",EDGE,"E8"),sQuery(id+"F2.wireOp",EDGE,"E10")])]}),"instanceName":"107"});
            var Q109;
            Q109=makeQuery(id+"F5.opPattern","COPY",BODY,{"derivedFrom":makeQuery(id+"F3.opExtrude","SWEPT_BODY",BODY,{"disambiguationData":[OSD([sQuery(id+"F2.wireOp",EDGE,"E2"),sQuery(id+"F2.wireOp",EDGE,"E3"),sQuery(id+"F2.wireOp",EDGE,"E4"),sQuery(id+"F2.wireOp",EDGE,"E5.filletArc"),sQuery(id+"F2.wireOp",EDGE,"E6.filletArc"),sQuery(id+"F2.wireOp",EDGE,"E7"),sQuery(id+"F2.wireOp",EDGE,"E8"),sQuery(id+"F2.wireOp",EDGE,"E10")])]}),"instanceName":"108"});
            var Q110;
            Q110=makeQuery(id+"F5.opPattern","COPY",BODY,{"derivedFrom":makeQuery(id+"F3.opExtrude","SWEPT_BODY",BODY,{"disambiguationData":[OSD([sQuery(id+"F2.wireOp",EDGE,"E2"),sQuery(id+"F2.wireOp",EDGE,"E3"),sQuery(id+"F2.wireOp",EDGE,"E4"),sQuery(id+"F2.wireOp",EDGE,"E5.filletArc"),sQuery(id+"F2.wireOp",EDGE,"E6.filletArc"),sQuery(id+"F2.wireOp",EDGE,"E7"),sQuery(id+"F2.wireOp",EDGE,"E8"),sQuery(id+"F2.wireOp",EDGE,"E10")])]}),"instanceName":"109"});
            var Q111;
            Q111=makeQuery(id+"F5.opPattern","COPY",BODY,{"derivedFrom":makeQuery(id+"F3.opExtrude","SWEPT_BODY",BODY,{"disambiguationData":[OSD([sQuery(id+"F2.wireOp",EDGE,"E2"),sQuery(id+"F2.wireOp",EDGE,"E3"),sQuery(id+"F2.wireOp",EDGE,"E4"),sQuery(id+"F2.wireOp",EDGE,"E5.filletArc"),sQuery(id+"F2.wireOp",EDGE,"E6.filletArc"),sQuery(id+"F2.wireOp",EDGE,"E7"),sQuery(id+"F2.wireOp",EDGE,"E8"),sQuery(id+"F2.wireOp",EDGE,"E10")])]}),"instanceName":"110"});
            var Q112;
            Q112=makeQuery(id+"F5.opPattern","COPY",BODY,{"derivedFrom":makeQuery(id+"F3.opExtrude","SWEPT_BODY",BODY,{"disambiguationData":[OSD([sQuery(id+"F2.wireOp",EDGE,"E2"),sQuery(id+"F2.wireOp",EDGE,"E3"),sQuery(id+"F2.wireOp",EDGE,"E4"),sQuery(id+"F2.wireOp",EDGE,"E5.filletArc"),sQuery(id+"F2.wireOp",EDGE,"E6.filletArc"),sQuery(id+"F2.wireOp",EDGE,"E7"),sQuery(id+"F2.wireOp",EDGE,"E8"),sQuery(id+"F2.wireOp",EDGE,"E10")])]}),"instanceName":"111"});
            var Q113;
            Q113=makeQuery(id+"F5.opPattern","COPY",BODY,{"derivedFrom":makeQuery(id+"F3.opExtrude","SWEPT_BODY",BODY,{"disambiguationData":[OSD([sQuery(id+"F2.wireOp",EDGE,"E2"),sQuery(id+"F2.wireOp",EDGE,"E3"),sQuery(id+"F2.wireOp",EDGE,"E4"),sQuery(id+"F2.wireOp",EDGE,"E5.filletArc"),sQuery(id+"F2.wireOp",EDGE,"E6.filletArc"),sQuery(id+"F2.wireOp",EDGE,"E7"),sQuery(id+"F2.wireOp",EDGE,"E8"),sQuery(id+"F2.wireOp",EDGE,"E10")])]}),"instanceName":"112"});
            var Q114;
            Q114=makeQuery(id+"F5.opPattern","COPY",BODY,{"derivedFrom":makeQuery(id+"F3.opExtrude","SWEPT_BODY",BODY,{"disambiguationData":[OSD([sQuery(id+"F2.wireOp",EDGE,"E2"),sQuery(id+"F2.wireOp",EDGE,"E3"),sQuery(id+"F2.wireOp",EDGE,"E4"),sQuery(id+"F2.wireOp",EDGE,"E5.filletArc"),sQuery(id+"F2.wireOp",EDGE,"E6.filletArc"),sQuery(id+"F2.wireOp",EDGE,"E7"),sQuery(id+"F2.wireOp",EDGE,"E8"),sQuery(id+"F2.wireOp",EDGE,"E10")])]}),"instanceName":"113"});
            var Q115;
            Q115=makeQuery(id+"F5.opPattern","COPY",BODY,{"derivedFrom":makeQuery(id+"F3.opExtrude","SWEPT_BODY",BODY,{"disambiguationData":[OSD([sQuery(id+"F2.wireOp",EDGE,"E2"),sQuery(id+"F2.wireOp",EDGE,"E3"),sQuery(id+"F2.wireOp",EDGE,"E4"),sQuery(id+"F2.wireOp",EDGE,"E5.filletArc"),sQuery(id+"F2.wireOp",EDGE,"E6.filletArc"),sQuery(id+"F2.wireOp",EDGE,"E7"),sQuery(id+"F2.wireOp",EDGE,"E8"),sQuery(id+"F2.wireOp",EDGE,"E10")])]}),"instanceName":"114"});
            var Q116;
            Q116=makeQuery(id+"F5.opPattern","COPY",BODY,{"derivedFrom":makeQuery(id+"F3.opExtrude","SWEPT_BODY",BODY,{"disambiguationData":[OSD([sQuery(id+"F2.wireOp",EDGE,"E2"),sQuery(id+"F2.wireOp",EDGE,"E3"),sQuery(id+"F2.wireOp",EDGE,"E4"),sQuery(id+"F2.wireOp",EDGE,"E5.filletArc"),sQuery(id+"F2.wireOp",EDGE,"E6.filletArc"),sQuery(id+"F2.wireOp",EDGE,"E7"),sQuery(id+"F2.wireOp",EDGE,"E8"),sQuery(id+"F2.wireOp",EDGE,"E10")])]}),"instanceName":"115"});
            var Q117;
            Q117=makeQuery(id+"F5.opPattern","COPY",BODY,{"derivedFrom":makeQuery(id+"F3.opExtrude","SWEPT_BODY",BODY,{"disambiguationData":[OSD([sQuery(id+"F2.wireOp",EDGE,"E2"),sQuery(id+"F2.wireOp",EDGE,"E3"),sQuery(id+"F2.wireOp",EDGE,"E4"),sQuery(id+"F2.wireOp",EDGE,"E5.filletArc"),sQuery(id+"F2.wireOp",EDGE,"E6.filletArc"),sQuery(id+"F2.wireOp",EDGE,"E7"),sQuery(id+"F2.wireOp",EDGE,"E8"),sQuery(id+"F2.wireOp",EDGE,"E10")])]}),"instanceName":"116"});
            var Q118;
            Q118=makeQuery(id+"F5.opPattern","COPY",BODY,{"derivedFrom":makeQuery(id+"F3.opExtrude","SWEPT_BODY",BODY,{"disambiguationData":[OSD([sQuery(id+"F2.wireOp",EDGE,"E2"),sQuery(id+"F2.wireOp",EDGE,"E3"),sQuery(id+"F2.wireOp",EDGE,"E4"),sQuery(id+"F2.wireOp",EDGE,"E5.filletArc"),sQuery(id+"F2.wireOp",EDGE,"E6.filletArc"),sQuery(id+"F2.wireOp",EDGE,"E7"),sQuery(id+"F2.wireOp",EDGE,"E8"),sQuery(id+"F2.wireOp",EDGE,"E10")])]}),"instanceName":"117"});
            var Q119;
            Q119=makeQuery(id+"F5.opPattern","COPY",BODY,{"derivedFrom":makeQuery(id+"F3.opExtrude","SWEPT_BODY",BODY,{"disambiguationData":[OSD([sQuery(id+"F2.wireOp",EDGE,"E2"),sQuery(id+"F2.wireOp",EDGE,"E3"),sQuery(id+"F2.wireOp",EDGE,"E4"),sQuery(id+"F2.wireOp",EDGE,"E5.filletArc"),sQuery(id+"F2.wireOp",EDGE,"E6.filletArc"),sQuery(id+"F2.wireOp",EDGE,"E7"),sQuery(id+"F2.wireOp",EDGE,"E8"),sQuery(id+"F2.wireOp",EDGE,"E10")])]}),"instanceName":"118"});
            var Q120;
            Q120=makeQuery(id+"F5.opPattern","COPY",BODY,{"derivedFrom":makeQuery(id+"F3.opExtrude","SWEPT_BODY",BODY,{"disambiguationData":[OSD([sQuery(id+"F2.wireOp",EDGE,"E2"),sQuery(id+"F2.wireOp",EDGE,"E3"),sQuery(id+"F2.wireOp",EDGE,"E4"),sQuery(id+"F2.wireOp",EDGE,"E5.filletArc"),sQuery(id+"F2.wireOp",EDGE,"E6.filletArc"),sQuery(id+"F2.wireOp",EDGE,"E7"),sQuery(id+"F2.wireOp",EDGE,"E8"),sQuery(id+"F2.wireOp",EDGE,"E10")])]}),"instanceName":"119"});
            var Q121;
            Q121=makeQuery(id+"F5.opPattern","COPY",BODY,{"derivedFrom":makeQuery(id+"F3.opExtrude","SWEPT_BODY",BODY,{"disambiguationData":[OSD([sQuery(id+"F2.wireOp",EDGE,"E2"),sQuery(id+"F2.wireOp",EDGE,"E3"),sQuery(id+"F2.wireOp",EDGE,"E4"),sQuery(id+"F2.wireOp",EDGE,"E5.filletArc"),sQuery(id+"F2.wireOp",EDGE,"E6.filletArc"),sQuery(id+"F2.wireOp",EDGE,"E7"),sQuery(id+"F2.wireOp",EDGE,"E8"),sQuery(id+"F2.wireOp",EDGE,"E10")])]}),"instanceName":"120"});
            var Q122;
            Q122=makeQuery(id+"F5.opPattern","COPY",BODY,{"derivedFrom":makeQuery(id+"F3.opExtrude","SWEPT_BODY",BODY,{"disambiguationData":[OSD([sQuery(id+"F2.wireOp",EDGE,"E2"),sQuery(id+"F2.wireOp",EDGE,"E3"),sQuery(id+"F2.wireOp",EDGE,"E4"),sQuery(id+"F2.wireOp",EDGE,"E5.filletArc"),sQuery(id+"F2.wireOp",EDGE,"E6.filletArc"),sQuery(id+"F2.wireOp",EDGE,"E7"),sQuery(id+"F2.wireOp",EDGE,"E8"),sQuery(id+"F2.wireOp",EDGE,"E10")])]}),"instanceName":"121"});
            var Q123;
            Q123=makeQuery(id+"F5.opPattern","COPY",BODY,{"derivedFrom":makeQuery(id+"F3.opExtrude","SWEPT_BODY",BODY,{"disambiguationData":[OSD([sQuery(id+"F2.wireOp",EDGE,"E2"),sQuery(id+"F2.wireOp",EDGE,"E3"),sQuery(id+"F2.wireOp",EDGE,"E4"),sQuery(id+"F2.wireOp",EDGE,"E5.filletArc"),sQuery(id+"F2.wireOp",EDGE,"E6.filletArc"),sQuery(id+"F2.wireOp",EDGE,"E7"),sQuery(id+"F2.wireOp",EDGE,"E8"),sQuery(id+"F2.wireOp",EDGE,"E10")])]}),"instanceName":"122"});
            var Q124;
            Q124=makeQuery(id+"F5.opPattern","COPY",BODY,{"derivedFrom":makeQuery(id+"F3.opExtrude","SWEPT_BODY",BODY,{"disambiguationData":[OSD([sQuery(id+"F2.wireOp",EDGE,"E2"),sQuery(id+"F2.wireOp",EDGE,"E3"),sQuery(id+"F2.wireOp",EDGE,"E4"),sQuery(id+"F2.wireOp",EDGE,"E5.filletArc"),sQuery(id+"F2.wireOp",EDGE,"E6.filletArc"),sQuery(id+"F2.wireOp",EDGE,"E7"),sQuery(id+"F2.wireOp",EDGE,"E8"),sQuery(id+"F2.wireOp",EDGE,"E10")])]}),"instanceName":"123"});
            var Q125;
            Q125=makeQuery(id+"F5.opPattern","COPY",BODY,{"derivedFrom":makeQuery(id+"F3.opExtrude","SWEPT_BODY",BODY,{"disambiguationData":[OSD([sQuery(id+"F2.wireOp",EDGE,"E2"),sQuery(id+"F2.wireOp",EDGE,"E3"),sQuery(id+"F2.wireOp",EDGE,"E4"),sQuery(id+"F2.wireOp",EDGE,"E5.filletArc"),sQuery(id+"F2.wireOp",EDGE,"E6.filletArc"),sQuery(id+"F2.wireOp",EDGE,"E7"),sQuery(id+"F2.wireOp",EDGE,"E8"),sQuery(id+"F2.wireOp",EDGE,"E10")])]}),"instanceName":"124"});
            var Q126;
            Q126=makeQuery(id+"F5.opPattern","COPY",BODY,{"derivedFrom":makeQuery(id+"F3.opExtrude","SWEPT_BODY",BODY,{"disambiguationData":[OSD([sQuery(id+"F2.wireOp",EDGE,"E2"),sQuery(id+"F2.wireOp",EDGE,"E3"),sQuery(id+"F2.wireOp",EDGE,"E4"),sQuery(id+"F2.wireOp",EDGE,"E5.filletArc"),sQuery(id+"F2.wireOp",EDGE,"E6.filletArc"),sQuery(id+"F2.wireOp",EDGE,"E7"),sQuery(id+"F2.wireOp",EDGE,"E8"),sQuery(id+"F2.wireOp",EDGE,"E10")])]}),"instanceName":"125"});
            var Q127;
            Q127=makeQuery(id+"F5.opPattern","COPY",BODY,{"derivedFrom":makeQuery(id+"F3.opExtrude","SWEPT_BODY",BODY,{"disambiguationData":[OSD([sQuery(id+"F2.wireOp",EDGE,"E2"),sQuery(id+"F2.wireOp",EDGE,"E3"),sQuery(id+"F2.wireOp",EDGE,"E4"),sQuery(id+"F2.wireOp",EDGE,"E5.filletArc"),sQuery(id+"F2.wireOp",EDGE,"E6.filletArc"),sQuery(id+"F2.wireOp",EDGE,"E7"),sQuery(id+"F2.wireOp",EDGE,"E8"),sQuery(id+"F2.wireOp",EDGE,"E10")])]}),"instanceName":"126"});
            var Q128;
            Q128=makeQuery(id+"F5.opPattern","COPY",BODY,{"derivedFrom":makeQuery(id+"F3.opExtrude","SWEPT_BODY",BODY,{"disambiguationData":[OSD([sQuery(id+"F2.wireOp",EDGE,"E2"),sQuery(id+"F2.wireOp",EDGE,"E3"),sQuery(id+"F2.wireOp",EDGE,"E4"),sQuery(id+"F2.wireOp",EDGE,"E5.filletArc"),sQuery(id+"F2.wireOp",EDGE,"E6.filletArc"),sQuery(id+"F2.wireOp",EDGE,"E7"),sQuery(id+"F2.wireOp",EDGE,"E8"),sQuery(id+"F2.wireOp",EDGE,"E10")])]}),"instanceName":"127"});
            booleanBodies(context, id + "F6", {"operationType" : BooleanOperationType.UNION, "tools" : qUnion([Q0, Q1, Q2, Q3, Q4, Q5, Q6, Q7, Q8, Q9, Q10, Q11, Q12, Q13, Q14, Q15, Q16, Q17, Q18, Q19, Q20, Q21, Q22, Q23, Q24, Q25, Q26, Q27, Q28, Q29, Q30, Q31, Q32, Q33, Q34, Q35, Q36, Q37, Q38, Q39, Q40, Q41, Q42, Q43, Q44, Q45, Q46, Q47, Q48, Q49, Q50, Q51, Q52, Q53, Q54, Q55, Q56, Q57, Q58, Q59, Q60, Q61, Q62, Q63, Q64, Q65, Q66, Q67, Q68, Q69, Q70, Q71, Q72, Q73, Q74, Q75, Q76, Q77, Q78, Q79, Q80, Q81, Q82, Q83, Q84, Q85, Q86, Q87, Q88, Q89, Q90, Q91, Q92, Q93, Q94, Q95, Q96, Q97, Q98, Q99, Q100, Q101, Q102, Q103, Q104, Q105, Q106, Q107, Q108, Q109, Q110, Q111, Q112, Q113, Q114, Q115, Q116, Q117, Q118, Q119, Q120, Q121, Q122, Q123, Q124, Q125, Q126, Q127, Q128])});
        }
        {
            var Q0;
            {var subQ0=sQuery(id+"F0.wireOp",EDGE,"E0");var subQ1=makeQuery(id+"F3.opExtrude","CAP_FACE",FACE,{"disambiguationData":[OSD([subQ0])],"isStart":false});Q0=makeQuery(id+"F6.opBoolean","MERGE",FACE,{"derivedFrom":[makeQuery(id+"F1.opExtrude","CAP_FACE",FACE,{"disambiguationData":[OSD([subQ0])],"isStart":false}),subQ1,makeQuery(id+"F5.opPattern","COPY",FACE,{"derivedFrom":subQ1,"instanceName":"1"}),makeQuery(id+"F5.opPattern","COPY",FACE,{"derivedFrom":subQ1,"instanceName":"2"}),makeQuery(id+"F5.opPattern","COPY",FACE,{"derivedFrom":subQ1,"instanceName":"3"}),makeQuery(id+"F5.opPattern","COPY",FACE,{"derivedFrom":subQ1,"instanceName":"4"}),makeQuery(id+"F5.opPattern","COPY",FACE,{"derivedFrom":subQ1,"instanceName":"5"}),makeQuery(id+"F5.opPattern","COPY",FACE,{"derivedFrom":subQ1,"instanceName":"6"}),makeQuery(id+"F5.opPattern","COPY",FACE,{"derivedFrom":subQ1,"instanceName":"7"}),makeQuery(id+"F5.opPattern","COPY",FACE,{"derivedFrom":subQ1,"instanceName":"8"}),makeQuery(id+"F5.opPattern","COPY",FACE,{"derivedFrom":subQ1,"instanceName":"9"}),makeQuery(id+"F5.opPattern","COPY",FACE,{"derivedFrom":subQ1,"instanceName":"10"}),makeQuery(id+"F5.opPattern","COPY",FACE,{"derivedFrom":subQ1,"instanceName":"11"}),makeQuery(id+"F5.opPattern","COPY",FACE,{"derivedFrom":subQ1,"instanceName":"12"}),makeQuery(id+"F5.opPattern","COPY",FACE,{"derivedFrom":subQ1,"instanceName":"13"}),makeQuery(id+"F5.opPattern","COPY",FACE,{"derivedFrom":subQ1,"instanceName":"14"}),makeQuery(id+"F5.opPattern","COPY",FACE,{"derivedFrom":subQ1,"instanceName":"15"}),makeQuery(id+"F5.opPattern","COPY",FACE,{"derivedFrom":subQ1,"instanceName":"16"}),makeQuery(id+"F5.opPattern","COPY",FACE,{"derivedFrom":subQ1,"instanceName":"17"}),makeQuery(id+"F5.opPattern","COPY",FACE,{"derivedFrom":subQ1,"instanceName":"18"}),makeQuery(id+"F5.opPattern","COPY",FACE,{"derivedFrom":subQ1,"instanceName":"19"}),makeQuery(id+"F5.opPattern","COPY",FACE,{"derivedFrom":subQ1,"instanceName":"20"}),makeQuery(id+"F5.opPattern","COPY",FACE,{"derivedFrom":subQ1,"instanceName":"21"}),makeQuery(id+"F5.opPattern","COPY",FACE,{"derivedFrom":subQ1,"instanceName":"22"}),makeQuery(id+"F5.opPattern","COPY",FACE,{"derivedFrom":subQ1,"instanceName":"23"}),makeQuery(id+"F5.opPattern","COPY",FACE,{"derivedFrom":subQ1,"instanceName":"24"}),makeQuery(id+"F5.opPattern","COPY",FACE,{"derivedFrom":subQ1,"instanceName":"25"}),makeQuery(id+"F5.opPattern","COPY",FACE,{"derivedFrom":subQ1,"instanceName":"26"}),makeQuery(id+"F5.opPattern","COPY",FACE,{"derivedFrom":subQ1,"instanceName":"27"}),makeQuery(id+"F5.opPattern","COPY",FACE,{"derivedFrom":subQ1,"instanceName":"28"}),makeQuery(id+"F5.opPattern","COPY",FACE,{"derivedFrom":subQ1,"instanceName":"29"}),makeQuery(id+"F5.opPattern","COPY",FACE,{"derivedFrom":subQ1,"instanceName":"30"}),makeQuery(id+"F5.opPattern","COPY",FACE,{"derivedFrom":subQ1,"instanceName":"31"}),makeQuery(id+"F5.opPattern","COPY",FACE,{"derivedFrom":subQ1,"instanceName":"32"}),makeQuery(id+"F5.opPattern","COPY",FACE,{"derivedFrom":subQ1,"instanceName":"33"}),makeQuery(id+"F5.opPattern","COPY",FACE,{"derivedFrom":subQ1,"instanceName":"34"}),makeQuery(id+"F5.opPattern","COPY",FACE,{"derivedFrom":subQ1,"instanceName":"35"}),makeQuery(id+"F5.opPattern","COPY",FACE,{"derivedFrom":subQ1,"instanceName":"36"}),makeQuery(id+"F5.opPattern","COPY",FACE,{"derivedFrom":subQ1,"instanceName":"37"}),makeQuery(id+"F5.opPattern","COPY",FACE,{"derivedFrom":subQ1,"instanceName":"38"}),makeQuery(id+"F5.opPattern","COPY",FACE,{"derivedFrom":subQ1,"instanceName":"39"}),makeQuery(id+"F5.opPattern","COPY",FACE,{"derivedFrom":subQ1,"instanceName":"40"}),makeQuery(id+"F5.opPattern","COPY",FACE,{"derivedFrom":subQ1,"instanceName":"41"}),makeQuery(id+"F5.opPattern","COPY",FACE,{"derivedFrom":subQ1,"instanceName":"42"}),makeQuery(id+"F5.opPattern","COPY",FACE,{"derivedFrom":subQ1,"instanceName":"43"}),makeQuery(id+"F5.opPattern","COPY",FACE,{"derivedFrom":subQ1,"instanceName":"44"}),makeQuery(id+"F5.opPattern","COPY",FACE,{"derivedFrom":subQ1,"instanceName":"45"}),makeQuery(id+"F5.opPattern","COPY",FACE,{"derivedFrom":subQ1,"instanceName":"46"}),makeQuery(id+"F5.opPattern","COPY",FACE,{"derivedFrom":subQ1,"instanceName":"47"}),makeQuery(id+"F5.opPattern","COPY",FACE,{"derivedFrom":subQ1,"instanceName":"48"}),makeQuery(id+"F5.opPattern","COPY",FACE,{"derivedFrom":subQ1,"instanceName":"49"}),makeQuery(id+"F5.opPattern","COPY",FACE,{"derivedFrom":subQ1,"instanceName":"50"}),makeQuery(id+"F5.opPattern","COPY",FACE,{"derivedFrom":subQ1,"instanceName":"51"}),makeQuery(id+"F5.opPattern","COPY",FACE,{"derivedFrom":subQ1,"instanceName":"52"}),makeQuery(id+"F5.opPattern","COPY",FACE,{"derivedFrom":subQ1,"instanceName":"53"}),makeQuery(id+"F5.opPattern","COPY",FACE,{"derivedFrom":subQ1,"instanceName":"54"}),makeQuery(id+"F5.opPattern","COPY",FACE,{"derivedFrom":subQ1,"instanceName":"55"}),makeQuery(id+"F5.opPattern","COPY",FACE,{"derivedFrom":subQ1,"instanceName":"56"}),makeQuery(id+"F5.opPattern","COPY",FACE,{"derivedFrom":subQ1,"instanceName":"57"}),makeQuery(id+"F5.opPattern","COPY",FACE,{"derivedFrom":subQ1,"instanceName":"58"}),makeQuery(id+"F5.opPattern","COPY",FACE,{"derivedFrom":subQ1,"instanceName":"59"}),makeQuery(id+"F5.opPattern","COPY",FACE,{"derivedFrom":subQ1,"instanceName":"60"}),makeQuery(id+"F5.opPattern","COPY",FACE,{"derivedFrom":subQ1,"instanceName":"61"}),makeQuery(id+"F5.opPattern","COPY",FACE,{"derivedFrom":subQ1,"instanceName":"62"}),makeQuery(id+"F5.opPattern","COPY",FACE,{"derivedFrom":subQ1,"instanceName":"63"}),makeQuery(id+"F5.opPattern","COPY",FACE,{"derivedFrom":subQ1,"instanceName":"64"}),makeQuery(id+"F5.opPattern","COPY",FACE,{"derivedFrom":subQ1,"instanceName":"65"}),makeQuery(id+"F5.opPattern","COPY",FACE,{"derivedFrom":subQ1,"instanceName":"66"}),makeQuery(id+"F5.opPattern","COPY",FACE,{"derivedFrom":subQ1,"instanceName":"67"}),makeQuery(id+"F5.opPattern","COPY",FACE,{"derivedFrom":subQ1,"instanceName":"68"}),makeQuery(id+"F5.opPattern","COPY",FACE,{"derivedFrom":subQ1,"instanceName":"69"}),makeQuery(id+"F5.opPattern","COPY",FACE,{"derivedFrom":subQ1,"instanceName":"70"}),makeQuery(id+"F5.opPattern","COPY",FACE,{"derivedFrom":subQ1,"instanceName":"71"}),makeQuery(id+"F5.opPattern","COPY",FACE,{"derivedFrom":subQ1,"instanceName":"72"}),makeQuery(id+"F5.opPattern","COPY",FACE,{"derivedFrom":subQ1,"instanceName":"73"}),makeQuery(id+"F5.opPattern","COPY",FACE,{"derivedFrom":subQ1,"instanceName":"74"}),makeQuery(id+"F5.opPattern","COPY",FACE,{"derivedFrom":subQ1,"instanceName":"75"}),makeQuery(id+"F5.opPattern","COPY",FACE,{"derivedFrom":subQ1,"instanceName":"76"}),makeQuery(id+"F5.opPattern","COPY",FACE,{"derivedFrom":subQ1,"instanceName":"77"}),makeQuery(id+"F5.opPattern","COPY",FACE,{"derivedFrom":subQ1,"instanceName":"78"}),makeQuery(id+"F5.opPattern","COPY",FACE,{"derivedFrom":subQ1,"instanceName":"79"}),makeQuery(id+"F5.opPattern","COPY",FACE,{"derivedFrom":subQ1,"instanceName":"80"}),makeQuery(id+"F5.opPattern","COPY",FACE,{"derivedFrom":subQ1,"instanceName":"81"}),makeQuery(id+"F5.opPattern","COPY",FACE,{"derivedFrom":subQ1,"instanceName":"82"}),makeQuery(id+"F5.opPattern","COPY",FACE,{"derivedFrom":subQ1,"instanceName":"83"}),makeQuery(id+"F5.opPattern","COPY",FACE,{"derivedFrom":subQ1,"instanceName":"84"}),makeQuery(id+"F5.opPattern","COPY",FACE,{"derivedFrom":subQ1,"instanceName":"85"}),makeQuery(id+"F5.opPattern","COPY",FACE,{"derivedFrom":subQ1,"instanceName":"86"}),makeQuery(id+"F5.opPattern","COPY",FACE,{"derivedFrom":subQ1,"instanceName":"87"}),makeQuery(id+"F5.opPattern","COPY",FACE,{"derivedFrom":subQ1,"instanceName":"88"}),makeQuery(id+"F5.opPattern","COPY",FACE,{"derivedFrom":subQ1,"instanceName":"89"}),makeQuery(id+"F5.opPattern","COPY",FACE,{"derivedFrom":subQ1,"instanceName":"90"}),makeQuery(id+"F5.opPattern","COPY",FACE,{"derivedFrom":subQ1,"instanceName":"91"}),makeQuery(id+"F5.opPattern","COPY",FACE,{"derivedFrom":subQ1,"instanceName":"92"}),makeQuery(id+"F5.opPattern","COPY",FACE,{"derivedFrom":subQ1,"instanceName":"93"}),makeQuery(id+"F5.opPattern","COPY",FACE,{"derivedFrom":subQ1,"instanceName":"94"}),makeQuery(id+"F5.opPattern","COPY",FACE,{"derivedFrom":subQ1,"instanceName":"95"}),makeQuery(id+"F5.opPattern","COPY",FACE,{"derivedFrom":subQ1,"instanceName":"96"}),makeQuery(id+"F5.opPattern","COPY",FACE,{"derivedFrom":subQ1,"instanceName":"97"}),makeQuery(id+"F5.opPattern","COPY",FACE,{"derivedFrom":subQ1,"instanceName":"98"}),makeQuery(id+"F5.opPattern","COPY",FACE,{"derivedFrom":subQ1,"instanceName":"99"}),makeQuery(id+"F5.opPattern","COPY",FACE,{"derivedFrom":subQ1,"instanceName":"100"}),makeQuery(id+"F5.opPattern","COPY",FACE,{"derivedFrom":subQ1,"instanceName":"101"}),makeQuery(id+"F5.opPattern","COPY",FACE,{"derivedFrom":subQ1,"instanceName":"102"}),makeQuery(id+"F5.opPattern","COPY",FACE,{"derivedFrom":subQ1,"instanceName":"103"}),makeQuery(id+"F5.opPattern","COPY",FACE,{"derivedFrom":subQ1,"instanceName":"104"}),makeQuery(id+"F5.opPattern","COPY",FACE,{"derivedFrom":subQ1,"instanceName":"105"}),makeQuery(id+"F5.opPattern","COPY",FACE,{"derivedFrom":subQ1,"instanceName":"106"}),makeQuery(id+"F5.opPattern","COPY",FACE,{"derivedFrom":subQ1,"instanceName":"107"}),makeQuery(id+"F5.opPattern","COPY",FACE,{"derivedFrom":subQ1,"instanceName":"108"}),makeQuery(id+"F5.opPattern","COPY",FACE,{"derivedFrom":subQ1,"instanceName":"109"}),makeQuery(id+"F5.opPattern","COPY",FACE,{"derivedFrom":subQ1,"instanceName":"110"}),makeQuery(id+"F5.opPattern","COPY",FACE,{"derivedFrom":subQ1,"instanceName":"111"}),makeQuery(id+"F5.opPattern","COPY",FACE,{"derivedFrom":subQ1,"instanceName":"112"}),makeQuery(id+"F5.opPattern","COPY",FACE,{"derivedFrom":subQ1,"instanceName":"113"}),makeQuery(id+"F5.opPattern","COPY",FACE,{"derivedFrom":subQ1,"instanceName":"114"}),makeQuery(id+"F5.opPattern","COPY",FACE,{"derivedFrom":subQ1,"instanceName":"115"}),makeQuery(id+"F5.opPattern","COPY",FACE,{"derivedFrom":subQ1,"instanceName":"116"}),makeQuery(id+"F5.opPattern","COPY",FACE,{"derivedFrom":subQ1,"instanceName":"117"}),makeQuery(id+"F5.opPattern","COPY",FACE,{"derivedFrom":subQ1,"instanceName":"118"}),makeQuery(id+"F5.opPattern","COPY",FACE,{"derivedFrom":subQ1,"instanceName":"119"}),makeQuery(id+"F5.opPattern","COPY",FACE,{"derivedFrom":subQ1,"instanceName":"120"}),makeQuery(id+"F5.opPattern","COPY",FACE,{"derivedFrom":subQ1,"instanceName":"121"}),makeQuery(id+"F5.opPattern","COPY",FACE,{"derivedFrom":subQ1,"instanceName":"122"}),makeQuery(id+"F5.opPattern","COPY",FACE,{"derivedFrom":subQ1,"instanceName":"123"}),makeQuery(id+"F5.opPattern","COPY",FACE,{"derivedFrom":subQ1,"instanceName":"124"}),makeQuery(id+"F5.opPattern","COPY",FACE,{"derivedFrom":subQ1,"instanceName":"125"}),makeQuery(id+"F5.opPattern","COPY",FACE,{"derivedFrom":subQ1,"instanceName":"126"}),makeQuery(id+"F5.opPattern","COPY",FACE,{"derivedFrom":subQ1,"instanceName":"127"})]});}
            var sketch = newSketch(context, id + "F7", { "sketchPlane" : qUnion([Q0])});
            skCircle(sketch, "E12", {"center": v(0, 0) * mm, "radius": 30.23 * mm});
            skSolve(sketch);
        }
        {
            var Q0;
            Q0=qSketchRegion(id+"F7",true);
            extrude(context, id + "F8", {"entities" : qUnion([Q0]), "operationType" : NewBodyOperationType.REMOVE, "oppositeDirection" : true, "depth" : 25.4 * mm});
        }
        {
            var Q0;
            {var subQ0=makeQuery(id+"F3.opExtrude","CAP_FACE",FACE,{"disambiguationData":[OSD([sQuery(id+"F2.wireOp",EDGE,"E2"),sQuery(id+"F2.wireOp",EDGE,"E3"),sQuery(id+"F2.wireOp",EDGE,"E4"),sQuery(id+"F2.wireOp",EDGE,"E5.filletArc"),sQuery(id+"F2.wireOp",EDGE,"E6.filletArc"),sQuery(id+"F2.wireOp",EDGE,"E7"),sQuery(id+"F2.wireOp",EDGE,"E8"),sQuery(id+"F2.wireOp",EDGE,"E10")])],"isStart":true});Q0=makeQuery(id+"F6.opBoolean","MERGE",FACE,{"derivedFrom":[makeQuery(id+"F1.opExtrude","CAP_FACE",FACE,{"disambiguationData":[OSD([sQuery(id+"F0.wireOp",EDGE,"E0")])],"isStart":true}),subQ0,makeQuery(id+"F5.opPattern","COPY",FACE,{"derivedFrom":subQ0,"instanceName":"1"}),makeQuery(id+"F5.opPattern","COPY",FACE,{"derivedFrom":subQ0,"instanceName":"2"}),makeQuery(id+"F5.opPattern","COPY",FACE,{"derivedFrom":subQ0,"instanceName":"3"}),makeQuery(id+"F5.opPattern","COPY",FACE,{"derivedFrom":subQ0,"instanceName":"4"}),makeQuery(id+"F5.opPattern","COPY",FACE,{"derivedFrom":subQ0,"instanceName":"5"}),makeQuery(id+"F5.opPattern","COPY",FACE,{"derivedFrom":subQ0,"instanceName":"6"}),makeQuery(id+"F5.opPattern","COPY",FACE,{"derivedFrom":subQ0,"instanceName":"7"}),makeQuery(id+"F5.opPattern","COPY",FACE,{"derivedFrom":subQ0,"instanceName":"8"}),makeQuery(id+"F5.opPattern","COPY",FACE,{"derivedFrom":subQ0,"instanceName":"9"}),makeQuery(id+"F5.opPattern","COPY",FACE,{"derivedFrom":subQ0,"instanceName":"10"}),makeQuery(id+"F5.opPattern","COPY",FACE,{"derivedFrom":subQ0,"instanceName":"11"}),makeQuery(id+"F5.opPattern","COPY",FACE,{"derivedFrom":subQ0,"instanceName":"12"}),makeQuery(id+"F5.opPattern","COPY",FACE,{"derivedFrom":subQ0,"instanceName":"13"}),makeQuery(id+"F5.opPattern","COPY",FACE,{"derivedFrom":subQ0,"instanceName":"14"}),makeQuery(id+"F5.opPattern","COPY",FACE,{"derivedFrom":subQ0,"instanceName":"15"}),makeQuery(id+"F5.opPattern","COPY",FACE,{"derivedFrom":subQ0,"instanceName":"16"}),makeQuery(id+"F5.opPattern","COPY",FACE,{"derivedFrom":subQ0,"instanceName":"17"}),makeQuery(id+"F5.opPattern","COPY",FACE,{"derivedFrom":subQ0,"instanceName":"18"}),makeQuery(id+"F5.opPattern","COPY",FACE,{"derivedFrom":subQ0,"instanceName":"19"}),makeQuery(id+"F5.opPattern","COPY",FACE,{"derivedFrom":subQ0,"instanceName":"20"}),makeQuery(id+"F5.opPattern","COPY",FACE,{"derivedFrom":subQ0,"instanceName":"21"}),makeQuery(id+"F5.opPattern","COPY",FACE,{"derivedFrom":subQ0,"instanceName":"22"}),makeQuery(id+"F5.opPattern","COPY",FACE,{"derivedFrom":subQ0,"instanceName":"23"}),makeQuery(id+"F5.opPattern","COPY",FACE,{"derivedFrom":subQ0,"instanceName":"24"}),makeQuery(id+"F5.opPattern","COPY",FACE,{"derivedFrom":subQ0,"instanceName":"25"}),makeQuery(id+"F5.opPattern","COPY",FACE,{"derivedFrom":subQ0,"instanceName":"26"}),makeQuery(id+"F5.opPattern","COPY",FACE,{"derivedFrom":subQ0,"instanceName":"27"}),makeQuery(id+"F5.opPattern","COPY",FACE,{"derivedFrom":subQ0,"instanceName":"28"}),makeQuery(id+"F5.opPattern","COPY",FACE,{"derivedFrom":subQ0,"instanceName":"29"}),makeQuery(id+"F5.opPattern","COPY",FACE,{"derivedFrom":subQ0,"instanceName":"30"}),makeQuery(id+"F5.opPattern","COPY",FACE,{"derivedFrom":subQ0,"instanceName":"31"}),makeQuery(id+"F5.opPattern","COPY",FACE,{"derivedFrom":subQ0,"instanceName":"32"}),makeQuery(id+"F5.opPattern","COPY",FACE,{"derivedFrom":subQ0,"instanceName":"33"}),makeQuery(id+"F5.opPattern","COPY",FACE,{"derivedFrom":subQ0,"instanceName":"34"}),makeQuery(id+"F5.opPattern","COPY",FACE,{"derivedFrom":subQ0,"instanceName":"35"}),makeQuery(id+"F5.opPattern","COPY",FACE,{"derivedFrom":subQ0,"instanceName":"36"}),makeQuery(id+"F5.opPattern","COPY",FACE,{"derivedFrom":subQ0,"instanceName":"37"}),makeQuery(id+"F5.opPattern","COPY",FACE,{"derivedFrom":subQ0,"instanceName":"38"}),makeQuery(id+"F5.opPattern","COPY",FACE,{"derivedFrom":subQ0,"instanceName":"39"}),makeQuery(id+"F5.opPattern","COPY",FACE,{"derivedFrom":subQ0,"instanceName":"40"}),makeQuery(id+"F5.opPattern","COPY",FACE,{"derivedFrom":subQ0,"instanceName":"41"}),makeQuery(id+"F5.opPattern","COPY",FACE,{"derivedFrom":subQ0,"instanceName":"42"}),makeQuery(id+"F5.opPattern","COPY",FACE,{"derivedFrom":subQ0,"instanceName":"43"}),makeQuery(id+"F5.opPattern","COPY",FACE,{"derivedFrom":subQ0,"instanceName":"44"}),makeQuery(id+"F5.opPattern","COPY",FACE,{"derivedFrom":subQ0,"instanceName":"45"}),makeQuery(id+"F5.opPattern","COPY",FACE,{"derivedFrom":subQ0,"instanceName":"46"}),makeQuery(id+"F5.opPattern","COPY",FACE,{"derivedFrom":subQ0,"instanceName":"47"}),makeQuery(id+"F5.opPattern","COPY",FACE,{"derivedFrom":subQ0,"instanceName":"48"}),makeQuery(id+"F5.opPattern","COPY",FACE,{"derivedFrom":subQ0,"instanceName":"49"}),makeQuery(id+"F5.opPattern","COPY",FACE,{"derivedFrom":subQ0,"instanceName":"50"}),makeQuery(id+"F5.opPattern","COPY",FACE,{"derivedFrom":subQ0,"instanceName":"51"}),makeQuery(id+"F5.opPattern","COPY",FACE,{"derivedFrom":subQ0,"instanceName":"52"}),makeQuery(id+"F5.opPattern","COPY",FACE,{"derivedFrom":subQ0,"instanceName":"53"}),makeQuery(id+"F5.opPattern","COPY",FACE,{"derivedFrom":subQ0,"instanceName":"54"}),makeQuery(id+"F5.opPattern","COPY",FACE,{"derivedFrom":subQ0,"instanceName":"55"}),makeQuery(id+"F5.opPattern","COPY",FACE,{"derivedFrom":subQ0,"instanceName":"56"}),makeQuery(id+"F5.opPattern","COPY",FACE,{"derivedFrom":subQ0,"instanceName":"57"}),makeQuery(id+"F5.opPattern","COPY",FACE,{"derivedFrom":subQ0,"instanceName":"58"}),makeQuery(id+"F5.opPattern","COPY",FACE,{"derivedFrom":subQ0,"instanceName":"59"}),makeQuery(id+"F5.opPattern","COPY",FACE,{"derivedFrom":subQ0,"instanceName":"60"}),makeQuery(id+"F5.opPattern","COPY",FACE,{"derivedFrom":subQ0,"instanceName":"61"}),makeQuery(id+"F5.opPattern","COPY",FACE,{"derivedFrom":subQ0,"instanceName":"62"}),makeQuery(id+"F5.opPattern","COPY",FACE,{"derivedFrom":subQ0,"instanceName":"63"}),makeQuery(id+"F5.opPattern","COPY",FACE,{"derivedFrom":subQ0,"instanceName":"64"}),makeQuery(id+"F5.opPattern","COPY",FACE,{"derivedFrom":subQ0,"instanceName":"65"}),makeQuery(id+"F5.opPattern","COPY",FACE,{"derivedFrom":subQ0,"instanceName":"66"}),makeQuery(id+"F5.opPattern","COPY",FACE,{"derivedFrom":subQ0,"instanceName":"67"}),makeQuery(id+"F5.opPattern","COPY",FACE,{"derivedFrom":subQ0,"instanceName":"68"}),makeQuery(id+"F5.opPattern","COPY",FACE,{"derivedFrom":subQ0,"instanceName":"69"}),makeQuery(id+"F5.opPattern","COPY",FACE,{"derivedFrom":subQ0,"instanceName":"70"}),makeQuery(id+"F5.opPattern","COPY",FACE,{"derivedFrom":subQ0,"instanceName":"71"}),makeQuery(id+"F5.opPattern","COPY",FACE,{"derivedFrom":subQ0,"instanceName":"72"}),makeQuery(id+"F5.opPattern","COPY",FACE,{"derivedFrom":subQ0,"instanceName":"73"}),makeQuery(id+"F5.opPattern","COPY",FACE,{"derivedFrom":subQ0,"instanceName":"74"}),makeQuery(id+"F5.opPattern","COPY",FACE,{"derivedFrom":subQ0,"instanceName":"75"}),makeQuery(id+"F5.opPattern","COPY",FACE,{"derivedFrom":subQ0,"instanceName":"76"}),makeQuery(id+"F5.opPattern","COPY",FACE,{"derivedFrom":subQ0,"instanceName":"77"}),makeQuery(id+"F5.opPattern","COPY",FACE,{"derivedFrom":subQ0,"instanceName":"78"}),makeQuery(id+"F5.opPattern","COPY",FACE,{"derivedFrom":subQ0,"instanceName":"79"}),makeQuery(id+"F5.opPattern","COPY",FACE,{"derivedFrom":subQ0,"instanceName":"80"}),makeQuery(id+"F5.opPattern","COPY",FACE,{"derivedFrom":subQ0,"instanceName":"81"}),makeQuery(id+"F5.opPattern","COPY",FACE,{"derivedFrom":subQ0,"instanceName":"82"}),makeQuery(id+"F5.opPattern","COPY",FACE,{"derivedFrom":subQ0,"instanceName":"83"}),makeQuery(id+"F5.opPattern","COPY",FACE,{"derivedFrom":subQ0,"instanceName":"84"}),makeQuery(id+"F5.opPattern","COPY",FACE,{"derivedFrom":subQ0,"instanceName":"85"}),makeQuery(id+"F5.opPattern","COPY",FACE,{"derivedFrom":subQ0,"instanceName":"86"}),makeQuery(id+"F5.opPattern","COPY",FACE,{"derivedFrom":subQ0,"instanceName":"87"}),makeQuery(id+"F5.opPattern","COPY",FACE,{"derivedFrom":subQ0,"instanceName":"88"}),makeQuery(id+"F5.opPattern","COPY",FACE,{"derivedFrom":subQ0,"instanceName":"89"}),makeQuery(id+"F5.opPattern","COPY",FACE,{"derivedFrom":subQ0,"instanceName":"90"}),makeQuery(id+"F5.opPattern","COPY",FACE,{"derivedFrom":subQ0,"instanceName":"91"}),makeQuery(id+"F5.opPattern","COPY",FACE,{"derivedFrom":subQ0,"instanceName":"92"}),makeQuery(id+"F5.opPattern","COPY",FACE,{"derivedFrom":subQ0,"instanceName":"93"}),makeQuery(id+"F5.opPattern","COPY",FACE,{"derivedFrom":subQ0,"instanceName":"94"}),makeQuery(id+"F5.opPattern","COPY",FACE,{"derivedFrom":subQ0,"instanceName":"95"}),makeQuery(id+"F5.opPattern","COPY",FACE,{"derivedFrom":subQ0,"instanceName":"96"}),makeQuery(id+"F5.opPattern","COPY",FACE,{"derivedFrom":subQ0,"instanceName":"97"}),makeQuery(id+"F5.opPattern","COPY",FACE,{"derivedFrom":subQ0,"instanceName":"98"}),makeQuery(id+"F5.opPattern","COPY",FACE,{"derivedFrom":subQ0,"instanceName":"99"}),makeQuery(id+"F5.opPattern","COPY",FACE,{"derivedFrom":subQ0,"instanceName":"100"}),makeQuery(id+"F5.opPattern","COPY",FACE,{"derivedFrom":subQ0,"instanceName":"101"}),makeQuery(id+"F5.opPattern","COPY",FACE,{"derivedFrom":subQ0,"instanceName":"102"}),makeQuery(id+"F5.opPattern","COPY",FACE,{"derivedFrom":subQ0,"instanceName":"103"}),makeQuery(id+"F5.opPattern","COPY",FACE,{"derivedFrom":subQ0,"instanceName":"104"}),makeQuery(id+"F5.opPattern","COPY",FACE,{"derivedFrom":subQ0,"instanceName":"105"}),makeQuery(id+"F5.opPattern","COPY",FACE,{"derivedFrom":subQ0,"instanceName":"106"}),makeQuery(id+"F5.opPattern","COPY",FACE,{"derivedFrom":subQ0,"instanceName":"107"}),makeQuery(id+"F5.opPattern","COPY",FACE,{"derivedFrom":subQ0,"instanceName":"108"}),makeQuery(id+"F5.opPattern","COPY",FACE,{"derivedFrom":subQ0,"instanceName":"109"}),makeQuery(id+"F5.opPattern","COPY",FACE,{"derivedFrom":subQ0,"instanceName":"110"}),makeQuery(id+"F5.opPattern","COPY",FACE,{"derivedFrom":subQ0,"instanceName":"111"}),makeQuery(id+"F5.opPattern","COPY",FACE,{"derivedFrom":subQ0,"instanceName":"112"}),makeQuery(id+"F5.opPattern","COPY",FACE,{"derivedFrom":subQ0,"instanceName":"113"}),makeQuery(id+"F5.opPattern","COPY",FACE,{"derivedFrom":subQ0,"instanceName":"114"}),makeQuery(id+"F5.opPattern","COPY",FACE,{"derivedFrom":subQ0,"instanceName":"115"}),makeQuery(id+"F5.opPattern","COPY",FACE,{"derivedFrom":subQ0,"instanceName":"116"}),makeQuery(id+"F5.opPattern","COPY",FACE,{"derivedFrom":subQ0,"instanceName":"117"}),makeQuery(id+"F5.opPattern","COPY",FACE,{"derivedFrom":subQ0,"instanceName":"118"}),makeQuery(id+"F5.opPattern","COPY",FACE,{"derivedFrom":subQ0,"instanceName":"119"}),makeQuery(id+"F5.opPattern","COPY",FACE,{"derivedFrom":subQ0,"instanceName":"120"}),makeQuery(id+"F5.opPattern","COPY",FACE,{"derivedFrom":subQ0,"instanceName":"121"}),makeQuery(id+"F5.opPattern","COPY",FACE,{"derivedFrom":subQ0,"instanceName":"122"}),makeQuery(id+"F5.opPattern","COPY",FACE,{"derivedFrom":subQ0,"instanceName":"123"}),makeQuery(id+"F5.opPattern","COPY",FACE,{"derivedFrom":subQ0,"instanceName":"124"}),makeQuery(id+"F5.opPattern","COPY",FACE,{"derivedFrom":subQ0,"instanceName":"125"}),makeQuery(id+"F5.opPattern","COPY",FACE,{"derivedFrom":subQ0,"instanceName":"126"}),makeQuery(id+"F5.opPattern","COPY",FACE,{"derivedFrom":subQ0,"instanceName":"127"})]});}
            var sketch = newSketch(context, id + "F9", { "sketchPlane" : qUnion([Q0])});
            skCircle(sketch, "E13", {"center": v(0, 0) * mm, "radius": 155.58 * mm});
            skCircle(sketch, "E14.0", {"center": v(0, 0) * mm, "radius": 30.23 * mm});
            skSolve(sketch);
        }
        {
            var Q0;
            Q0 = qSketchRegion(id + "F9", true);
            extrude(context, id + "F10", {"entities" : qUnion([Q0]), "operationType" : NewBodyOperationType.ADD, "depth" : 17.53 * mm});
        }
        {
            var Q0;
            {var subQ0=sQuery(id+"F0.wireOp",EDGE,"E0");var subQ1=makeQuery(id+"F3.opExtrude","CAP_FACE",FACE,{"disambiguationData":[OSD([subQ0])],"isStart":false});Q0=makeQuery(id+"F6.opBoolean","MERGE",FACE,{"derivedFrom":[makeQuery(id+"F1.opExtrude","CAP_FACE",FACE,{"disambiguationData":[OSD([subQ0])],"isStart":false}),subQ1,makeQuery(id+"F5.opPattern","COPY",FACE,{"derivedFrom":subQ1,"instanceName":"1"}),makeQuery(id+"F5.opPattern","COPY",FACE,{"derivedFrom":subQ1,"instanceName":"2"}),makeQuery(id+"F5.opPattern","COPY",FACE,{"derivedFrom":subQ1,"instanceName":"3"}),makeQuery(id+"F5.opPattern","COPY",FACE,{"derivedFrom":subQ1,"instanceName":"4"}),makeQuery(id+"F5.opPattern","COPY",FACE,{"derivedFrom":subQ1,"instanceName":"5"}),makeQuery(id+"F5.opPattern","COPY",FACE,{"derivedFrom":subQ1,"instanceName":"6"}),makeQuery(id+"F5.opPattern","COPY",FACE,{"derivedFrom":subQ1,"instanceName":"7"}),makeQuery(id+"F5.opPattern","COPY",FACE,{"derivedFrom":subQ1,"instanceName":"8"}),makeQuery(id+"F5.opPattern","COPY",FACE,{"derivedFrom":subQ1,"instanceName":"9"}),makeQuery(id+"F5.opPattern","COPY",FACE,{"derivedFrom":subQ1,"instanceName":"10"}),makeQuery(id+"F5.opPattern","COPY",FACE,{"derivedFrom":subQ1,"instanceName":"11"}),makeQuery(id+"F5.opPattern","COPY",FACE,{"derivedFrom":subQ1,"instanceName":"12"}),makeQuery(id+"F5.opPattern","COPY",FACE,{"derivedFrom":subQ1,"instanceName":"13"}),makeQuery(id+"F5.opPattern","COPY",FACE,{"derivedFrom":subQ1,"instanceName":"14"}),makeQuery(id+"F5.opPattern","COPY",FACE,{"derivedFrom":subQ1,"instanceName":"15"}),makeQuery(id+"F5.opPattern","COPY",FACE,{"derivedFrom":subQ1,"instanceName":"16"}),makeQuery(id+"F5.opPattern","COPY",FACE,{"derivedFrom":subQ1,"instanceName":"17"}),makeQuery(id+"F5.opPattern","COPY",FACE,{"derivedFrom":subQ1,"instanceName":"18"}),makeQuery(id+"F5.opPattern","COPY",FACE,{"derivedFrom":subQ1,"instanceName":"19"}),makeQuery(id+"F5.opPattern","COPY",FACE,{"derivedFrom":subQ1,"instanceName":"20"}),makeQuery(id+"F5.opPattern","COPY",FACE,{"derivedFrom":subQ1,"instanceName":"21"}),makeQuery(id+"F5.opPattern","COPY",FACE,{"derivedFrom":subQ1,"instanceName":"22"}),makeQuery(id+"F5.opPattern","COPY",FACE,{"derivedFrom":subQ1,"instanceName":"23"}),makeQuery(id+"F5.opPattern","COPY",FACE,{"derivedFrom":subQ1,"instanceName":"24"}),makeQuery(id+"F5.opPattern","COPY",FACE,{"derivedFrom":subQ1,"instanceName":"25"}),makeQuery(id+"F5.opPattern","COPY",FACE,{"derivedFrom":subQ1,"instanceName":"26"}),makeQuery(id+"F5.opPattern","COPY",FACE,{"derivedFrom":subQ1,"instanceName":"27"}),makeQuery(id+"F5.opPattern","COPY",FACE,{"derivedFrom":subQ1,"instanceName":"28"}),makeQuery(id+"F5.opPattern","COPY",FACE,{"derivedFrom":subQ1,"instanceName":"29"}),makeQuery(id+"F5.opPattern","COPY",FACE,{"derivedFrom":subQ1,"instanceName":"30"}),makeQuery(id+"F5.opPattern","COPY",FACE,{"derivedFrom":subQ1,"instanceName":"31"}),makeQuery(id+"F5.opPattern","COPY",FACE,{"derivedFrom":subQ1,"instanceName":"32"}),makeQuery(id+"F5.opPattern","COPY",FACE,{"derivedFrom":subQ1,"instanceName":"33"}),makeQuery(id+"F5.opPattern","COPY",FACE,{"derivedFrom":subQ1,"instanceName":"34"}),makeQuery(id+"F5.opPattern","COPY",FACE,{"derivedFrom":subQ1,"instanceName":"35"}),makeQuery(id+"F5.opPattern","COPY",FACE,{"derivedFrom":subQ1,"instanceName":"36"}),makeQuery(id+"F5.opPattern","COPY",FACE,{"derivedFrom":subQ1,"instanceName":"37"}),makeQuery(id+"F5.opPattern","COPY",FACE,{"derivedFrom":subQ1,"instanceName":"38"}),makeQuery(id+"F5.opPattern","COPY",FACE,{"derivedFrom":subQ1,"instanceName":"39"}),makeQuery(id+"F5.opPattern","COPY",FACE,{"derivedFrom":subQ1,"instanceName":"40"}),makeQuery(id+"F5.opPattern","COPY",FACE,{"derivedFrom":subQ1,"instanceName":"41"}),makeQuery(id+"F5.opPattern","COPY",FACE,{"derivedFrom":subQ1,"instanceName":"42"}),makeQuery(id+"F5.opPattern","COPY",FACE,{"derivedFrom":subQ1,"instanceName":"43"}),makeQuery(id+"F5.opPattern","COPY",FACE,{"derivedFrom":subQ1,"instanceName":"44"}),makeQuery(id+"F5.opPattern","COPY",FACE,{"derivedFrom":subQ1,"instanceName":"45"}),makeQuery(id+"F5.opPattern","COPY",FACE,{"derivedFrom":subQ1,"instanceName":"46"}),makeQuery(id+"F5.opPattern","COPY",FACE,{"derivedFrom":subQ1,"instanceName":"47"}),makeQuery(id+"F5.opPattern","COPY",FACE,{"derivedFrom":subQ1,"instanceName":"48"}),makeQuery(id+"F5.opPattern","COPY",FACE,{"derivedFrom":subQ1,"instanceName":"49"}),makeQuery(id+"F5.opPattern","COPY",FACE,{"derivedFrom":subQ1,"instanceName":"50"}),makeQuery(id+"F5.opPattern","COPY",FACE,{"derivedFrom":subQ1,"instanceName":"51"}),makeQuery(id+"F5.opPattern","COPY",FACE,{"derivedFrom":subQ1,"instanceName":"52"}),makeQuery(id+"F5.opPattern","COPY",FACE,{"derivedFrom":subQ1,"instanceName":"53"}),makeQuery(id+"F5.opPattern","COPY",FACE,{"derivedFrom":subQ1,"instanceName":"54"}),makeQuery(id+"F5.opPattern","COPY",FACE,{"derivedFrom":subQ1,"instanceName":"55"}),makeQuery(id+"F5.opPattern","COPY",FACE,{"derivedFrom":subQ1,"instanceName":"56"}),makeQuery(id+"F5.opPattern","COPY",FACE,{"derivedFrom":subQ1,"instanceName":"57"}),makeQuery(id+"F5.opPattern","COPY",FACE,{"derivedFrom":subQ1,"instanceName":"58"}),makeQuery(id+"F5.opPattern","COPY",FACE,{"derivedFrom":subQ1,"instanceName":"59"}),makeQuery(id+"F5.opPattern","COPY",FACE,{"derivedFrom":subQ1,"instanceName":"60"}),makeQuery(id+"F5.opPattern","COPY",FACE,{"derivedFrom":subQ1,"instanceName":"61"}),makeQuery(id+"F5.opPattern","COPY",FACE,{"derivedFrom":subQ1,"instanceName":"62"}),makeQuery(id+"F5.opPattern","COPY",FACE,{"derivedFrom":subQ1,"instanceName":"63"}),makeQuery(id+"F5.opPattern","COPY",FACE,{"derivedFrom":subQ1,"instanceName":"64"}),makeQuery(id+"F5.opPattern","COPY",FACE,{"derivedFrom":subQ1,"instanceName":"65"}),makeQuery(id+"F5.opPattern","COPY",FACE,{"derivedFrom":subQ1,"instanceName":"66"}),makeQuery(id+"F5.opPattern","COPY",FACE,{"derivedFrom":subQ1,"instanceName":"67"}),makeQuery(id+"F5.opPattern","COPY",FACE,{"derivedFrom":subQ1,"instanceName":"68"}),makeQuery(id+"F5.opPattern","COPY",FACE,{"derivedFrom":subQ1,"instanceName":"69"}),makeQuery(id+"F5.opPattern","COPY",FACE,{"derivedFrom":subQ1,"instanceName":"70"}),makeQuery(id+"F5.opPattern","COPY",FACE,{"derivedFrom":subQ1,"instanceName":"71"}),makeQuery(id+"F5.opPattern","COPY",FACE,{"derivedFrom":subQ1,"instanceName":"72"}),makeQuery(id+"F5.opPattern","COPY",FACE,{"derivedFrom":subQ1,"instanceName":"73"}),makeQuery(id+"F5.opPattern","COPY",FACE,{"derivedFrom":subQ1,"instanceName":"74"}),makeQuery(id+"F5.opPattern","COPY",FACE,{"derivedFrom":subQ1,"instanceName":"75"}),makeQuery(id+"F5.opPattern","COPY",FACE,{"derivedFrom":subQ1,"instanceName":"76"}),makeQuery(id+"F5.opPattern","COPY",FACE,{"derivedFrom":subQ1,"instanceName":"77"}),makeQuery(id+"F5.opPattern","COPY",FACE,{"derivedFrom":subQ1,"instanceName":"78"}),makeQuery(id+"F5.opPattern","COPY",FACE,{"derivedFrom":subQ1,"instanceName":"79"}),makeQuery(id+"F5.opPattern","COPY",FACE,{"derivedFrom":subQ1,"instanceName":"80"}),makeQuery(id+"F5.opPattern","COPY",FACE,{"derivedFrom":subQ1,"instanceName":"81"}),makeQuery(id+"F5.opPattern","COPY",FACE,{"derivedFrom":subQ1,"instanceName":"82"}),makeQuery(id+"F5.opPattern","COPY",FACE,{"derivedFrom":subQ1,"instanceName":"83"}),makeQuery(id+"F5.opPattern","COPY",FACE,{"derivedFrom":subQ1,"instanceName":"84"}),makeQuery(id+"F5.opPattern","COPY",FACE,{"derivedFrom":subQ1,"instanceName":"85"}),makeQuery(id+"F5.opPattern","COPY",FACE,{"derivedFrom":subQ1,"instanceName":"86"}),makeQuery(id+"F5.opPattern","COPY",FACE,{"derivedFrom":subQ1,"instanceName":"87"}),makeQuery(id+"F5.opPattern","COPY",FACE,{"derivedFrom":subQ1,"instanceName":"88"}),makeQuery(id+"F5.opPattern","COPY",FACE,{"derivedFrom":subQ1,"instanceName":"89"}),makeQuery(id+"F5.opPattern","COPY",FACE,{"derivedFrom":subQ1,"instanceName":"90"}),makeQuery(id+"F5.opPattern","COPY",FACE,{"derivedFrom":subQ1,"instanceName":"91"}),makeQuery(id+"F5.opPattern","COPY",FACE,{"derivedFrom":subQ1,"instanceName":"92"}),makeQuery(id+"F5.opPattern","COPY",FACE,{"derivedFrom":subQ1,"instanceName":"93"}),makeQuery(id+"F5.opPattern","COPY",FACE,{"derivedFrom":subQ1,"instanceName":"94"}),makeQuery(id+"F5.opPattern","COPY",FACE,{"derivedFrom":subQ1,"instanceName":"95"}),makeQuery(id+"F5.opPattern","COPY",FACE,{"derivedFrom":subQ1,"instanceName":"96"}),makeQuery(id+"F5.opPattern","COPY",FACE,{"derivedFrom":subQ1,"instanceName":"97"}),makeQuery(id+"F5.opPattern","COPY",FACE,{"derivedFrom":subQ1,"instanceName":"98"}),makeQuery(id+"F5.opPattern","COPY",FACE,{"derivedFrom":subQ1,"instanceName":"99"}),makeQuery(id+"F5.opPattern","COPY",FACE,{"derivedFrom":subQ1,"instanceName":"100"}),makeQuery(id+"F5.opPattern","COPY",FACE,{"derivedFrom":subQ1,"instanceName":"101"}),makeQuery(id+"F5.opPattern","COPY",FACE,{"derivedFrom":subQ1,"instanceName":"102"}),makeQuery(id+"F5.opPattern","COPY",FACE,{"derivedFrom":subQ1,"instanceName":"103"}),makeQuery(id+"F5.opPattern","COPY",FACE,{"derivedFrom":subQ1,"instanceName":"104"}),makeQuery(id+"F5.opPattern","COPY",FACE,{"derivedFrom":subQ1,"instanceName":"105"}),makeQuery(id+"F5.opPattern","COPY",FACE,{"derivedFrom":subQ1,"instanceName":"106"}),makeQuery(id+"F5.opPattern","COPY",FACE,{"derivedFrom":subQ1,"instanceName":"107"}),makeQuery(id+"F5.opPattern","COPY",FACE,{"derivedFrom":subQ1,"instanceName":"108"}),makeQuery(id+"F5.opPattern","COPY",FACE,{"derivedFrom":subQ1,"instanceName":"109"}),makeQuery(id+"F5.opPattern","COPY",FACE,{"derivedFrom":subQ1,"instanceName":"110"}),makeQuery(id+"F5.opPattern","COPY",FACE,{"derivedFrom":subQ1,"instanceName":"111"}),makeQuery(id+"F5.opPattern","COPY",FACE,{"derivedFrom":subQ1,"instanceName":"112"}),makeQuery(id+"F5.opPattern","COPY",FACE,{"derivedFrom":subQ1,"instanceName":"113"}),makeQuery(id+"F5.opPattern","COPY",FACE,{"derivedFrom":subQ1,"instanceName":"114"}),makeQuery(id+"F5.opPattern","COPY",FACE,{"derivedFrom":subQ1,"instanceName":"115"}),makeQuery(id+"F5.opPattern","COPY",FACE,{"derivedFrom":subQ1,"instanceName":"116"}),makeQuery(id+"F5.opPattern","COPY",FACE,{"derivedFrom":subQ1,"instanceName":"117"}),makeQuery(id+"F5.opPattern","COPY",FACE,{"derivedFrom":subQ1,"instanceName":"118"}),makeQuery(id+"F5.opPattern","COPY",FACE,{"derivedFrom":subQ1,"instanceName":"119"}),makeQuery(id+"F5.opPattern","COPY",FACE,{"derivedFrom":subQ1,"instanceName":"120"}),makeQuery(id+"F5.opPattern","COPY",FACE,{"derivedFrom":subQ1,"instanceName":"121"}),makeQuery(id+"F5.opPattern","COPY",FACE,{"derivedFrom":subQ1,"instanceName":"122"}),makeQuery(id+"F5.opPattern","COPY",FACE,{"derivedFrom":subQ1,"instanceName":"123"}),makeQuery(id+"F5.opPattern","COPY",FACE,{"derivedFrom":subQ1,"instanceName":"124"}),makeQuery(id+"F5.opPattern","COPY",FACE,{"derivedFrom":subQ1,"instanceName":"125"}),makeQuery(id+"F5.opPattern","COPY",FACE,{"derivedFrom":subQ1,"instanceName":"126"}),makeQuery(id+"F5.opPattern","COPY",FACE,{"derivedFrom":subQ1,"instanceName":"127"})]});}
            var sketch = newSketch(context, id + "F11", { "sketchPlane" : qUnion([Q0])});
            skCircle(sketch, "E15.0", {"center": v(0, 0) * mm, "radius": 155.58 * mm});
            skCircle(sketch, "E16.0", {"center": v(0, 0) * mm, "radius": 30.23 * mm});
            skSolve(sketch);
        }
        {
            var Q0;
            Q0 = qSketchRegion(id + "F11", true);
            extrude(context, id + "F12", {"entities" : qUnion([Q0]), "operationType" : NewBodyOperationType.ADD, "depth" : 17.53 * mm});
        }
    });
